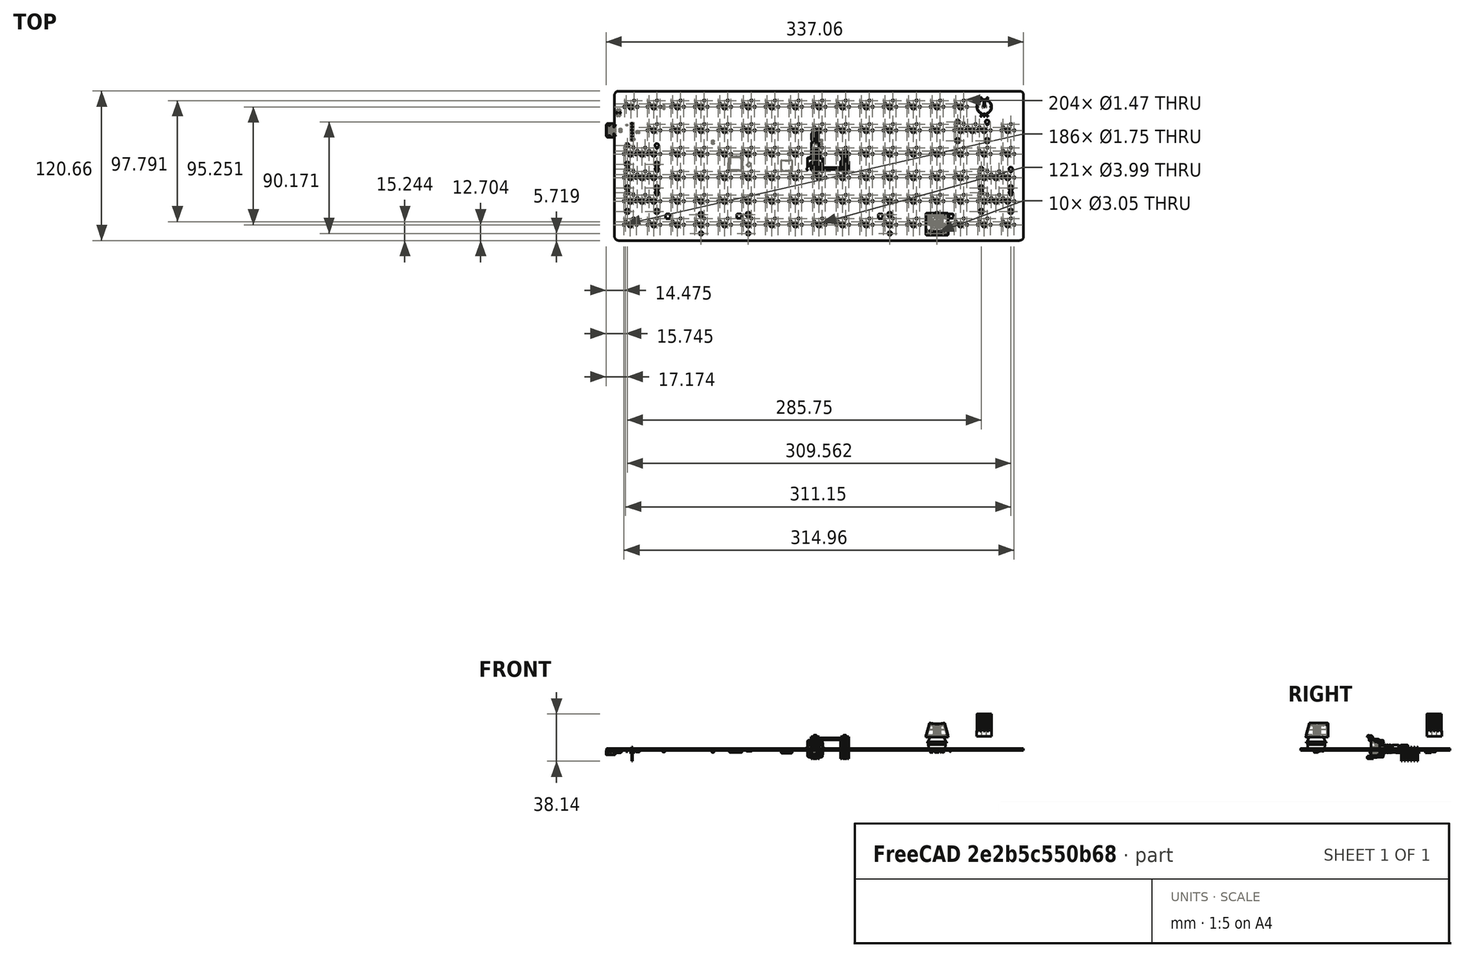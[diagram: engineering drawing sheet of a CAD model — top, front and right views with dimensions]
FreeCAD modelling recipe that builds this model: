
FCSTD DOCUMENT  (FreeCAD 0.19R24291 (Git))
Label: Orthonite87_002
License: All rights reserved
LicenseURL: http://en.wikipedia.org/wiki/All_rights_reserved
objects: App::Link×376, Part::Feature×31, App::Part×8, PartDesign::CoordinateSystem×1, Sketcher::SketchObject×1
note: 33 computed .brp shape members not serialized (recipe doc carries the construction recipe); baked Part::Feature solids carry a one-line shape summary decoded from their .brp

FEATURE [PartDesign::CoordinateSystem] Local_CS_e1db
  AttacherType = Attacher::AttachEngine3D
FEATURE [Part::Feature] Pcb_e1db
  Placement = pos=(-174.625,80.9625,0) rot=(0,0,1;0rad)
  shape: bbox 336.6 x 120.7 x 1.6 mm, 675 faces (baked)
FEATURE [Sketcher::SketchObject] PCB_Sketch_e1db
  FullyConstrained = false
  sketch-geometry (18):
    g0: LineSegment StartX=-168.275 StartY=33.3375 StartZ=0 EndX=-168.275 EndY=23.8125 EndZ=0
    g1: LineSegment StartX=-163.512 StartY=23.0188 StartZ=0 EndX=-162.719 EndY=23.0188 EndZ=0
    g2: LineSegment StartX=-163.512 StartY=34.1313 StartZ=0 EndX=-162.719 EndY=34.1313 EndZ=0
    g3: LineSegment StartX=-167.481 StartY=34.1313 StartZ=0 EndX=-163.512 EndY=34.1313 EndZ=0
    g4: LineSegment StartX=-163.512 StartY=23.0188 StartZ=0 EndX=-167.481 EndY=23.0188 EndZ=0
    g5: LineSegment StartX=-161.925 StartY=22.225 StartZ=0 EndX=-161.925 EndY=-57.15 EndZ=0
    g6: LineSegment StartX=-161.925 StartY=57.15 StartZ=0 EndX=-161.925 EndY=34.925 EndZ=0
    g7: LineSegment StartX=168.275 StartY=-57.15 StartZ=0 EndX=168.275 EndY=57.15 EndZ=0
    g8: LineSegment StartX=-158.75 StartY=-60.325 StartZ=0 EndX=165.1 EndY=-60.325 EndZ=0
    g9: LineSegment StartX=-158.75 StartY=60.325 StartZ=0 EndX=165.1 EndY=60.325 EndZ=0
    g10: ArcOfCircle CenterX=-167.481 CenterY=33.3375 CenterZ=0 NormalX=0 NormalY=0 NormalZ=1 AngleXU=0 Radius=0.79375 StartAngle=1.5708 EndAngle=3.14159
    g11: ArcOfCircle CenterX=-167.481 CenterY=23.8125 CenterZ=0 NormalX=0 NormalY=0 NormalZ=1 AngleXU=0 Radius=0.79375 StartAngle=3.14159 EndAngle=4.71239
    g12: ArcOfCircle CenterX=-162.719 CenterY=22.225 CenterZ=0 NormalX=0 NormalY=0 NormalZ=1 AngleXU=0 Radius=0.79375 StartAngle=0 EndAngle=1.5708
    g13: ArcOfCircle CenterX=-162.719 CenterY=34.925 CenterZ=0 NormalX=0 NormalY=0 NormalZ=1 AngleXU=0 Radius=0.79375 StartAngle=4.71239 EndAngle=6.28319
    g14: ArcOfCircle CenterX=165.1 CenterY=-57.15 CenterZ=0 NormalX=0 NormalY=0 NormalZ=1 AngleXU=0 Radius=3.175 StartAngle=4.71239 EndAngle=6.28319
    g15: ArcOfCircle CenterX=-158.75 CenterY=-57.15 CenterZ=0 NormalX=0 NormalY=0 NormalZ=1 AngleXU=0 Radius=3.175 StartAngle=3.14159 EndAngle=4.71239
    g16: ArcOfCircle CenterX=-158.75 CenterY=57.15 CenterZ=0 NormalX=0 NormalY=0 NormalZ=1 AngleXU=0 Radius=3.175 StartAngle=1.5708 EndAngle=3.14159
    g17: ArcOfCircle CenterX=165.1 CenterY=57.15 CenterZ=0 NormalX=0 NormalY=0 NormalZ=1 AngleXU=0 Radius=3.175 StartAngle=0 EndAngle=1.5708
FEATURE [Part::Feature] Shape  label="K_105_cherry mx_611CBFA4"
  Placement = pos=(98.425,-47.6255,5.5) rot=(0,0.707107,0.707107;3.14159rad)
  shape: bbox 15.64 x 16.33 x 17.85 mm, 92 faces (baked)
FEATURE [Part::Feature] Shape001  label="K_105_MX 轴标准键帽__¨¹_¡À__¡§1__¨¤_611CBFA4[2]"
  Placement = pos=(89.425,-38.1255,9.5) rot=(1,0,0;1.5708rad)
  shape: bbox 18.01 x 18 x 11.38 mm, 348 faces (baked)
FEATURE [App::Link] K_105_cherry_mx_611CBFA4_ln_  label="K_108_105_cherry mx_611DE0BA"
  LinkPlacement = pos=(155.575,-47.6255,5.5) rot=(0,0.707107,0.707107;3.14159rad)
  LinkedObject = -> Shape
  Placement = pos=(155.575,-47.6255,5.5) rot=(0,0.707107,0.707107;3.14159rad)
FEATURE [App::Link] K_105_MX______________________________________1_______611CBFA4_2__ln_  label="K_108_105_MX 轴标准键帽__¨¹_¡À__¡§1__¨¤_611DE0BA[2]"
  LinkPlacement = pos=(146.575,-38.1255,9.5) rot=(1,0,0;1.5708rad)
  LinkedObject = -> Shape001
  Placement = pos=(146.575,-38.1255,9.5) rot=(1,0,0;1.5708rad)
FEATURE [App::Link] K_105_cherry_mx_611CBFA4_ln_001  label="K_107_105_cherry mx_611DE0A5"
  LinkPlacement = pos=(136.525,-47.6255,5.5) rot=(0,0.707107,0.707107;3.14159rad)
  LinkedObject = -> Shape
  Placement = pos=(136.525,-47.6255,5.5) rot=(0,0.707107,0.707107;3.14159rad)
FEATURE [App::Link] K_105_MX______________________________________1_______611CBFA4_2__ln_001  label="K_107_105_MX 轴标准键帽__¨¹_¡À__¡§1__¨¤_611DE0A5[2]"
  LinkPlacement = pos=(127.525,-38.1255,9.5) rot=(1,0,0;1.5708rad)
  LinkedObject = -> Shape001
  Placement = pos=(127.525,-38.1255,9.5) rot=(1,0,0;1.5708rad)
FEATURE [App::Link] K_105_cherry_mx_611CBFA4_ln_002  label="K_106_105_cherry mx_611DE090"
  LinkPlacement = pos=(117.475,-47.6255,5.5) rot=(0,0.707107,0.707107;3.14159rad)
  LinkedObject = -> Shape
  Placement = pos=(117.475,-47.6255,5.5) rot=(0,0.707107,0.707107;3.14159rad)
FEATURE [App::Link] K_105_MX______________________________________1_______611CBFA4_2__ln_002  label="K_106_105_MX 轴标准键帽__¨¹_¡À__¡§1__¨¤_611DE090[2]"
  LinkPlacement = pos=(108.475,-38.1255,9.5) rot=(1,0,0;1.5708rad)
  LinkedObject = -> Shape001
  Placement = pos=(108.475,-38.1255,9.5) rot=(1,0,0;1.5708rad)
FEATURE [App::Link] K_105_cherry_mx_611CBFA4_ln_003  label="K_103_105_cherry mx_611DE023"
  LinkPlacement = pos=(60.325,-47.6255,5.5) rot=(0,0.707107,0.707107;3.14159rad)
  LinkedObject = -> Shape
  Placement = pos=(60.325,-47.6255,5.5) rot=(0,0.707107,0.707107;3.14159rad)
FEATURE [App::Link] K_105_MX______________________________________1_______611CBFA4_2__ln_003  label="K_103_105_MX 轴标准键帽__¨¹_¡À__¡§1__¨¤_611DE023[2]"
  LinkPlacement = pos=(51.325,-38.1255,9.5) rot=(1,0,0;1.5708rad)
  LinkedObject = -> Shape001
  Placement = pos=(51.325,-38.1255,9.5) rot=(1,0,0;1.5708rad)
FEATURE [App::Link] K_105_cherry_mx_611CBFA4_ln_004  label="K_102_105_cherry mx_611DE00E"
  LinkPlacement = pos=(41.275,-47.6255,5.5) rot=(0,0.707107,0.707107;3.14159rad)
  LinkedObject = -> Shape
  Placement = pos=(41.275,-47.6255,5.5) rot=(0,0.707107,0.707107;3.14159rad)
FEATURE [App::Link] K_105_MX______________________________________1_______611CBFA4_2__ln_004  label="K_102_105_MX 轴标准键帽__¨¹_¡À__¡§1__¨¤_611DE00E[2]"
  LinkPlacement = pos=(32.275,-38.1255,9.5) rot=(1,0,0;1.5708rad)
  LinkedObject = -> Shape001
  Placement = pos=(32.275,-38.1255,9.5) rot=(1,0,0;1.5708rad)
FEATURE [App::Link] K_105_cherry_mx_611CBFA4_ln_005  label="K_101_105_cherry mx_611DDFF9"
  LinkPlacement = pos=(22.225,-47.6255,5.5) rot=(0,0.707107,0.707107;3.14159rad)
  LinkedObject = -> Shape
  Placement = pos=(22.225,-47.6255,5.5) rot=(0,0.707107,0.707107;3.14159rad)
FEATURE [App::Link] K_105_MX______________________________________1_______611CBFA4_2__ln_005  label="K_101_105_MX 轴标准键帽__¨¹_¡À__¡§1__¨¤_611DDFF9[2]"
  LinkPlacement = pos=(13.225,-38.1255,9.5) rot=(1,0,0;1.5708rad)
  LinkedObject = -> Shape001
  Placement = pos=(13.225,-38.1255,9.5) rot=(1,0,0;1.5708rad)
FEATURE [App::Link] K_105_cherry_mx_611CBFA4_ln_006  label="K_100_105_cherry mx_611DDFE4"
  LinkPlacement = pos=(3.175,-47.6255,5.5) rot=(0,0.707107,0.707107;3.14159rad)
  LinkedObject = -> Shape
  Placement = pos=(3.175,-47.6255,5.5) rot=(0,0.707107,0.707107;3.14159rad)
FEATURE [App::Link] K_105_MX______________________________________1_______611CBFA4_2__ln_006  label="K_100_105_MX 轴标准键帽__¨¹_¡À__¡§1__¨¤_611DDFE4[2]"
  LinkPlacement = pos=(-5.825,-38.1255,9.5) rot=(1,0,0;1.5708rad)
  LinkedObject = -> Shape001
  Placement = pos=(-5.825,-38.1255,9.5) rot=(1,0,0;1.5708rad)
FEATURE [App::Link] K_105_cherry_mx_611CBFA4_ln_007  label="K_2_105_cherry mx_611DD732"
  LinkPlacement = pos=(-148.717,47.625,5.5) rot=(0,0.707107,0.707107;3.14159rad)
  LinkedObject = -> Shape
  Placement = pos=(-148.717,47.625,5.5) rot=(0,0.707107,0.707107;3.14159rad)
FEATURE [App::Link] K_105_MX______________________________________1_______611CBFA4_2__ln_007  label="K_2_105_MX 轴标准键帽__¨¹_¡À__¡§1__¨¤_611DD732[2]"
  LinkPlacement = pos=(-157.717,57.125,9.5) rot=(1,0,0;1.5708rad)
  LinkedObject = -> Shape001
  Placement = pos=(-157.717,57.125,9.5) rot=(1,0,0;1.5708rad)
FEATURE [App::Link] K_105_cherry_mx_611CBFA4_ln_008  label="K_9_105_cherry mx_611DD7C5"
  LinkPlacement = pos=(-15.875,47.625,5.5) rot=(0,0.707107,0.707107;3.14159rad)
  LinkedObject = -> Shape
  Placement = pos=(-15.875,47.625,5.5) rot=(0,0.707107,0.707107;3.14159rad)
FEATURE [App::Link] K_105_MX______________________________________1_______611CBFA4_2__ln_008  label="K_9_105_MX 轴标准键帽__¨¹_¡À__¡§1__¨¤_611DD7C5[2]"
  LinkPlacement = pos=(-24.875,57.125,9.5) rot=(1,0,0;1.5708rad)
  LinkedObject = -> Shape001
  Placement = pos=(-24.875,57.125,9.5) rot=(1,0,0;1.5708rad)
FEATURE [App::Link] K_105_cherry_mx_611CBFA4_ln_009  label="K_8_105_cherry mx_611DD7B0"
  LinkPlacement = pos=(-34.925,47.625,5.5) rot=(0,0.707107,0.707107;3.14159rad)
  LinkedObject = -> Shape
  Placement = pos=(-34.925,47.625,5.5) rot=(0,0.707107,0.707107;3.14159rad)
FEATURE [App::Link] K_105_MX______________________________________1_______611CBFA4_2__ln_009  label="K_8_105_MX 轴标准键帽__¨¹_¡À__¡§1__¨¤_611DD7B0[2]"
  LinkPlacement = pos=(-43.925,57.125,9.5) rot=(1,0,0;1.5708rad)
  LinkedObject = -> Shape001
  Placement = pos=(-43.925,57.125,9.5) rot=(1,0,0;1.5708rad)
FEATURE [App::Link] K_105_cherry_mx_611CBFA4_ln_010  label="K_7_105_cherry mx_611DD79B"
  LinkPlacement = pos=(-53.975,47.625,5.5) rot=(0,0.707107,0.707107;3.14159rad)
  LinkedObject = -> Shape
  Placement = pos=(-53.975,47.625,5.5) rot=(0,0.707107,0.707107;3.14159rad)
FEATURE [App::Link] K_105_MX______________________________________1_______611CBFA4_2__ln_010  label="K_7_105_MX 轴标准键帽__¨¹_¡À__¡§1__¨¤_611DD79B[2]"
  LinkPlacement = pos=(-62.975,57.125,9.5) rot=(1,0,0;1.5708rad)
  LinkedObject = -> Shape001
  Placement = pos=(-62.975,57.125,9.5) rot=(1,0,0;1.5708rad)
FEATURE [App::Link] K_105_cherry_mx_611CBFA4_ln_011  label="K_6_105_cherry mx_611DD786"
  LinkPlacement = pos=(-73.025,47.625,5.5) rot=(0,0.707107,0.707107;3.14159rad)
  LinkedObject = -> Shape
  Placement = pos=(-73.025,47.625,5.5) rot=(0,0.707107,0.707107;3.14159rad)
FEATURE [App::Link] K_105_MX______________________________________1_______611CBFA4_2__ln_011  label="K_6_105_MX 轴标准键帽__¨¹_¡À__¡§1__¨¤_611DD786[2]"
  LinkPlacement = pos=(-82.025,57.125,9.5) rot=(1,0,0;1.5708rad)
  LinkedObject = -> Shape001
  Placement = pos=(-82.025,57.125,9.5) rot=(1,0,0;1.5708rad)
FEATURE [App::Link] K_105_cherry_mx_611CBFA4_ln_012  label="K_5_105_cherry mx_611DD771"
  LinkPlacement = pos=(-92.075,47.625,5.5) rot=(0,0.707107,0.707107;3.14159rad)
  LinkedObject = -> Shape
  Placement = pos=(-92.075,47.625,5.5) rot=(0,0.707107,0.707107;3.14159rad)
FEATURE [App::Link] K_105_MX______________________________________1_______611CBFA4_2__ln_012  label="K_5_105_MX 轴标准键帽__¨¹_¡À__¡§1__¨¤_611DD771[2]"
  LinkPlacement = pos=(-101.075,57.125,9.5) rot=(1,0,0;1.5708rad)
  LinkedObject = -> Shape001
  Placement = pos=(-101.075,57.125,9.5) rot=(1,0,0;1.5708rad)
FEATURE [App::Link] K_105_cherry_mx_611CBFA4_ln_013  label="K_4_105_cherry mx_611DD75C"
  LinkPlacement = pos=(-111.125,47.625,5.5) rot=(0,0.707107,0.707107;3.14159rad)
  LinkedObject = -> Shape
  Placement = pos=(-111.125,47.625,5.5) rot=(0,0.707107,0.707107;3.14159rad)
FEATURE [App::Link] K_105_MX______________________________________1_______611CBFA4_2__ln_013  label="K_4_105_MX 轴标准键帽__¨¹_¡À__¡§1__¨¤_611DD75C[2]"
  LinkPlacement = pos=(-120.125,57.125,9.5) rot=(1,0,0;1.5708rad)
  LinkedObject = -> Shape001
  Placement = pos=(-120.125,57.125,9.5) rot=(1,0,0;1.5708rad)
FEATURE [App::Link] K_105_cherry_mx_611CBFA4_ln_014  label="K_3_105_cherry mx_611DD747"
  LinkPlacement = pos=(-130.175,47.625,5.5) rot=(0,0.707107,0.707107;3.14159rad)
  LinkedObject = -> Shape
  Placement = pos=(-130.175,47.625,5.5) rot=(0,0.707107,0.707107;3.14159rad)
FEATURE [App::Link] K_105_MX______________________________________1_______611CBFA4_2__ln_014  label="K_3_105_MX 轴标准键帽__¨¹_¡À__¡§1__¨¤_611DD747[2]"
  LinkPlacement = pos=(-139.175,57.125,9.5) rot=(1,0,0;1.5708rad)
  LinkedObject = -> Shape001
  Placement = pos=(-139.175,57.125,9.5) rot=(1,0,0;1.5708rad)
FEATURE [App::Link] K_105_cherry_mx_611CBFA4_ln_015  label="K_33_105_cherry mx_611E8F84"
  LinkPlacement = pos=(155.575,28.575,5.5) rot=(0,0.707107,0.707107;3.14159rad)
  LinkedObject = -> Shape
  Placement = pos=(155.575,28.575,5.5) rot=(0,0.707107,0.707107;3.14159rad)
FEATURE [App::Link] K_105_MX______________________________________1_______611CBFA4_2__ln_015  label="K_33_105_MX 轴标准键帽__¨¹_¡À__¡§1__¨¤_611E8F84[2]"
  LinkPlacement = pos=(146.575,38.075,9.5) rot=(1,0,0;1.5708rad)
  LinkedObject = -> Shape001
  Placement = pos=(146.575,38.075,9.5) rot=(1,0,0;1.5708rad)
FEATURE [App::Link] K_105_cherry_mx_611CBFA4_ln_016  label="K_99_105_cherry mx_611DDFCF"
  LinkPlacement = pos=(-15.875,-47.6255,5.5) rot=(0,0.707107,0.707107;3.14159rad)
  LinkedObject = -> Shape
  Placement = pos=(-15.875,-47.6255,5.5) rot=(0,0.707107,0.707107;3.14159rad)
FEATURE [App::Link] K_105_MX______________________________________1_______611CBFA4_2__ln_016  label="K_99_105_MX 轴标准键帽__¨¹_¡À__¡§1__¨¤_611DDFCF[2]"
  LinkPlacement = pos=(-24.875,-38.1255,9.5) rot=(1,0,0;1.5708rad)
  LinkedObject = -> Shape001
  Placement = pos=(-24.875,-38.1255,9.5) rot=(1,0,0;1.5708rad)
FEATURE [App::Link] K_105_cherry_mx_611CBFA4_ln_017  label="K_98_105_cherry mx_611DDFBA"
  LinkPlacement = pos=(-34.925,-47.6255,5.5) rot=(0,0.707107,0.707107;3.14159rad)
  LinkedObject = -> Shape
  Placement = pos=(-34.925,-47.6255,5.5) rot=(0,0.707107,0.707107;3.14159rad)
FEATURE [App::Link] K_105_MX______________________________________1_______611CBFA4_2__ln_017  label="K_98_105_MX 轴标准键帽__¨¹_¡À__¡§1__¨¤_611DDFBA[2]"
  LinkPlacement = pos=(-43.925,-38.1255,9.5) rot=(1,0,0;1.5708rad)
  LinkedObject = -> Shape001
  Placement = pos=(-43.925,-38.1255,9.5) rot=(1,0,0;1.5708rad)
FEATURE [App::Link] K_105_cherry_mx_611CBFA4_ln_018  label="K_97_105_cherry mx_611DDFA5"
  LinkPlacement = pos=(-53.975,-47.6255,5.5) rot=(0,0.707107,0.707107;3.14159rad)
  LinkedObject = -> Shape
  Placement = pos=(-53.975,-47.6255,5.5) rot=(0,0.707107,0.707107;3.14159rad)
FEATURE [App::Link] K_105_MX______________________________________1_______611CBFA4_2__ln_018  label="K_97_105_MX 轴标准键帽__¨¹_¡À__¡§1__¨¤_611DDFA5[2]"
  LinkPlacement = pos=(-62.975,-38.1255,9.5) rot=(1,0,0;1.5708rad)
  LinkedObject = -> Shape001
  Placement = pos=(-62.975,-38.1255,9.5) rot=(1,0,0;1.5708rad)
FEATURE [App::Link] K_105_cherry_mx_611CBFA4_ln_019  label="K_95_105_cherry mx_611DDF60"
  LinkPlacement = pos=(-92.075,-47.6255,5.5) rot=(0,0.707107,0.707107;3.14159rad)
  LinkedObject = -> Shape
  Placement = pos=(-92.075,-47.6255,5.5) rot=(0,0.707107,0.707107;3.14159rad)
FEATURE [App::Link] K_105_MX______________________________________1_______611CBFA4_2__ln_019  label="K_95_105_MX 轴标准键帽__¨¹_¡À__¡§1__¨¤_611DDF60[2]"
  LinkPlacement = pos=(-101.075,-38.1255,9.5) rot=(1,0,0;1.5708rad)
  LinkedObject = -> Shape001
  Placement = pos=(-101.075,-38.1255,9.5) rot=(1,0,0;1.5708rad)
FEATURE [App::Link] K_105_cherry_mx_611CBFA4_ln_020  label="K_94_105_cherry mx_611DDF4B"
  LinkPlacement = pos=(-111.125,-47.6255,5.5) rot=(0,0.707107,0.707107;3.14159rad)
  LinkedObject = -> Shape
  Placement = pos=(-111.125,-47.6255,5.5) rot=(0,0.707107,0.707107;3.14159rad)
FEATURE [App::Link] K_105_MX______________________________________1_______611CBFA4_2__ln_020  label="K_94_105_MX 轴标准键帽__¨¹_¡À__¡§1__¨¤_611DDF4B[2]"
  LinkPlacement = pos=(-120.125,-38.1255,9.5) rot=(1,0,0;1.5708rad)
  LinkedObject = -> Shape001
  Placement = pos=(-120.125,-38.1255,9.5) rot=(1,0,0;1.5708rad)
FEATURE [App::Link] K_105_cherry_mx_611CBFA4_ln_021  label="K_93_105_cherry mx_611DDF36"
  LinkPlacement = pos=(-130.175,-47.6255,5.5) rot=(0,0.707107,0.707107;3.14159rad)
  LinkedObject = -> Shape
  Placement = pos=(-130.175,-47.6255,5.5) rot=(0,0.707107,0.707107;3.14159rad)
FEATURE [App::Link] K_105_MX______________________________________1_______611CBFA4_2__ln_021  label="K_93_105_MX 轴标准键帽__¨¹_¡À__¡§1__¨¤_611DDF36[2]"
  LinkPlacement = pos=(-139.175,-38.1255,9.5) rot=(1,0,0;1.5708rad)
  LinkedObject = -> Shape001
  Placement = pos=(-139.175,-38.1255,9.5) rot=(1,0,0;1.5708rad)
FEATURE [App::Link] K_105_cherry_mx_611CBFA4_ln_022  label="K_92_105_cherry mx_611DDF21"
  LinkPlacement = pos=(-149.225,-47.6255,5.5) rot=(0,0.707107,0.707107;3.14159rad)
  LinkedObject = -> Shape
  Placement = pos=(-149.225,-47.6255,5.5) rot=(0,0.707107,0.707107;3.14159rad)
FEATURE [App::Link] K_105_MX______________________________________1_______611CBFA4_2__ln_022  label="K_92_105_MX 轴标准键帽__¨¹_¡À__¡§1__¨¤_611DDF21[2]"
  LinkPlacement = pos=(-158.225,-38.1255,9.5) rot=(1,0,0;1.5708rad)
  LinkedObject = -> Shape001
  Placement = pos=(-158.225,-38.1255,9.5) rot=(1,0,0;1.5708rad)
FEATURE [App::Link] K_105_cherry_mx_611CBFA4_ln_023  label="K_88_105_cherry mx_611DDEB2"
  LinkPlacement = pos=(136.525,-28.5755,5.5) rot=(0,0.707107,0.707107;3.14159rad)
  LinkedObject = -> Shape
  Placement = pos=(136.525,-28.5755,5.5) rot=(0,0.707107,0.707107;3.14159rad)
FEATURE [App::Link] K_105_MX______________________________________1_______611CBFA4_2__ln_023  label="K_88_105_MX 轴标准键帽__¨¹_¡À__¡§1__¨¤_611DDEB2[2]"
  LinkPlacement = pos=(127.525,-19.0755,9.5) rot=(1,0,0;1.5708rad)
  LinkedObject = -> Shape001
  Placement = pos=(127.525,-19.0755,9.5) rot=(1,0,0;1.5708rad)
FEATURE [App::Link] K_105_cherry_mx_611CBFA4_ln_024  label="K_87_105_cherry mx_611DDE9D"
  LinkPlacement = pos=(117.475,-28.5755,5.5) rot=(0,0.707107,0.707107;3.14159rad)
  LinkedObject = -> Shape
  Placement = pos=(117.475,-28.5755,5.5) rot=(0,0.707107,0.707107;3.14159rad)
FEATURE [App::Link] K_105_MX______________________________________1_______611CBFA4_2__ln_024  label="K_87_105_MX 轴标准键帽__¨¹_¡À__¡§1__¨¤_611DDE9D[2]"
  LinkPlacement = pos=(108.475,-19.0755,9.5) rot=(1,0,0;1.5708rad)
  LinkedObject = -> Shape001
  Placement = pos=(108.475,-19.0755,9.5) rot=(1,0,0;1.5708rad)
FEATURE [App::Link] K_105_cherry_mx_611CBFA4_ln_025  label="K_86_105_cherry mx_611DDE88"
  LinkPlacement = pos=(98.425,-28.5755,5.5) rot=(0,0.707107,0.707107;3.14159rad)
  LinkedObject = -> Shape
  Placement = pos=(98.425,-28.5755,5.5) rot=(0,0.707107,0.707107;3.14159rad)
FEATURE [App::Link] K_105_MX______________________________________1_______611CBFA4_2__ln_025  label="K_86_105_MX 轴标准键帽__¨¹_¡À__¡§1__¨¤_611DDE88[2]"
  LinkPlacement = pos=(89.425,-19.0755,9.5) rot=(1,0,0;1.5708rad)
  LinkedObject = -> Shape001
  Placement = pos=(89.425,-19.0755,9.5) rot=(1,0,0;1.5708rad)
FEATURE [App::Link] K_105_cherry_mx_611CBFA4_ln_026  label="K_85_105_cherry mx_611DDE73"
  LinkPlacement = pos=(79.375,-28.5755,5.5) rot=(0,0.707107,0.707107;3.14159rad)
  LinkedObject = -> Shape
  Placement = pos=(79.375,-28.5755,5.5) rot=(0,0.707107,0.707107;3.14159rad)
FEATURE [App::Link] K_105_MX______________________________________1_______611CBFA4_2__ln_026  label="K_85_105_MX 轴标准键帽__¨¹_¡À__¡§1__¨¤_611DDE73[2]"
  LinkPlacement = pos=(70.375,-19.0755,9.5) rot=(1,0,0;1.5708rad)
  LinkedObject = -> Shape001
  Placement = pos=(70.375,-19.0755,9.5) rot=(1,0,0;1.5708rad)
FEATURE [App::Link] K_105_cherry_mx_611CBFA4_ln_027  label="K_84_105_cherry mx_611DDE5E"
  LinkPlacement = pos=(60.325,-28.5755,5.5) rot=(0,0.707107,0.707107;3.14159rad)
  LinkedObject = -> Shape
  Placement = pos=(60.325,-28.5755,5.5) rot=(0,0.707107,0.707107;3.14159rad)
FEATURE [App::Link] K_105_MX______________________________________1_______611CBFA4_2__ln_027  label="K_84_105_MX 轴标准键帽__¨¹_¡À__¡§1__¨¤_611DDE5E[2]"
  LinkPlacement = pos=(51.325,-19.0755,9.5) rot=(1,0,0;1.5708rad)
  LinkedObject = -> Shape001
  Placement = pos=(51.325,-19.0755,9.5) rot=(1,0,0;1.5708rad)
FEATURE [App::Link] K_105_cherry_mx_611CBFA4_ln_028  label="K_83_105_cherry mx_611DDE49"
  LinkPlacement = pos=(41.275,-28.5755,5.5) rot=(0,0.707107,0.707107;3.14159rad)
  LinkedObject = -> Shape
  Placement = pos=(41.275,-28.5755,5.5) rot=(0,0.707107,0.707107;3.14159rad)
FEATURE [App::Link] K_105_MX______________________________________1_______611CBFA4_2__ln_028  label="K_83_105_MX 轴标准键帽__¨¹_¡À__¡§1__¨¤_611DDE49[2]"
  LinkPlacement = pos=(32.275,-19.0755,9.5) rot=(1,0,0;1.5708rad)
  LinkedObject = -> Shape001
  Placement = pos=(32.275,-19.0755,9.5) rot=(1,0,0;1.5708rad)
FEATURE [App::Link] K_105_cherry_mx_611CBFA4_ln_029  label="K_82_105_cherry mx_611DDE34"
  LinkPlacement = pos=(22.225,-28.5755,5.5) rot=(0,0.707107,0.707107;3.14159rad)
  LinkedObject = -> Shape
  Placement = pos=(22.225,-28.5755,5.5) rot=(0,0.707107,0.707107;3.14159rad)
FEATURE [App::Link] K_105_MX______________________________________1_______611CBFA4_2__ln_029  label="K_82_105_MX 轴标准键帽__¨¹_¡À__¡§1__¨¤_611DDE34[2]"
  LinkPlacement = pos=(13.225,-19.0755,9.5) rot=(1,0,0;1.5708rad)
  LinkedObject = -> Shape001
  Placement = pos=(13.225,-19.0755,9.5) rot=(1,0,0;1.5708rad)
FEATURE [App::Link] K_105_cherry_mx_611CBFA4_ln_030  label="K_81_105_cherry mx_611DDE1F"
  LinkPlacement = pos=(3.175,-28.5755,5.5) rot=(0,0.707107,0.707107;3.14159rad)
  LinkedObject = -> Shape
  Placement = pos=(3.175,-28.5755,5.5) rot=(0,0.707107,0.707107;3.14159rad)
FEATURE [App::Link] K_105_MX______________________________________1_______611CBFA4_2__ln_030  label="K_81_105_MX 轴标准键帽__¨¹_¡À__¡§1__¨¤_611DDE1F[2]"
  LinkPlacement = pos=(-5.825,-19.0755,9.5) rot=(1,0,0;1.5708rad)
  LinkedObject = -> Shape001
  Placement = pos=(-5.825,-19.0755,9.5) rot=(1,0,0;1.5708rad)
FEATURE [App::Link] K_105_cherry_mx_611CBFA4_ln_031  label="K_80_105_cherry mx_611DDE0A"
  LinkPlacement = pos=(-15.875,-28.5755,5.5) rot=(0,0.707107,0.707107;3.14159rad)
  LinkedObject = -> Shape
  Placement = pos=(-15.875,-28.5755,5.5) rot=(0,0.707107,0.707107;3.14159rad)
FEATURE [App::Link] K_105_MX______________________________________1_______611CBFA4_2__ln_031  label="K_80_105_MX 轴标准键帽__¨¹_¡À__¡§1__¨¤_611DDE0A[2]"
  LinkPlacement = pos=(-24.875,-19.0755,9.5) rot=(1,0,0;1.5708rad)
  LinkedObject = -> Shape001
  Placement = pos=(-24.875,-19.0755,9.5) rot=(1,0,0;1.5708rad)
FEATURE [App::Link] K_105_cherry_mx_611CBFA4_ln_032  label="K_79_105_cherry mx_611DDDF5"
  LinkPlacement = pos=(-34.925,-28.5755,5.5) rot=(0,0.707107,0.707107;3.14159rad)
  LinkedObject = -> Shape
  Placement = pos=(-34.925,-28.5755,5.5) rot=(0,0.707107,0.707107;3.14159rad)
FEATURE [App::Link] K_105_MX______________________________________1_______611CBFA4_2__ln_032  label="K_79_105_MX 轴标准键帽__¨¹_¡À__¡§1__¨¤_611DDDF5[2]"
  LinkPlacement = pos=(-43.925,-19.0755,9.5) rot=(1,0,0;1.5708rad)
  LinkedObject = -> Shape001
  Placement = pos=(-43.925,-19.0755,9.5) rot=(1,0,0;1.5708rad)
FEATURE [App::Link] K_105_cherry_mx_611CBFA4_ln_033  label="K_78_105_cherry mx_611DDDE0"
  LinkPlacement = pos=(-53.975,-28.5755,5.5) rot=(0,0.707107,0.707107;3.14159rad)
  LinkedObject = -> Shape
  Placement = pos=(-53.975,-28.5755,5.5) rot=(0,0.707107,0.707107;3.14159rad)
FEATURE [App::Link] K_105_MX______________________________________1_______611CBFA4_2__ln_033  label="K_78_105_MX 轴标准键帽__¨¹_¡À__¡§1__¨¤_611DDDE0[2]"
  LinkPlacement = pos=(-62.975,-19.0755,9.5) rot=(1,0,0;1.5708rad)
  LinkedObject = -> Shape001
  Placement = pos=(-62.975,-19.0755,9.5) rot=(1,0,0;1.5708rad)
FEATURE [App::Link] K_105_cherry_mx_611CBFA4_ln_034  label="K_77_105_cherry mx_611DDDCB"
  LinkPlacement = pos=(-73.025,-28.5755,5.5) rot=(0,0.707107,0.707107;3.14159rad)
  LinkedObject = -> Shape
  Placement = pos=(-73.025,-28.5755,5.5) rot=(0,0.707107,0.707107;3.14159rad)
FEATURE [App::Link] K_105_MX______________________________________1_______611CBFA4_2__ln_034  label="K_77_105_MX 轴标准键帽__¨¹_¡À__¡§1__¨¤_611DDDCB[2]"
  LinkPlacement = pos=(-82.025,-19.0755,9.5) rot=(1,0,0;1.5708rad)
  LinkedObject = -> Shape001
  Placement = pos=(-82.025,-19.0755,9.5) rot=(1,0,0;1.5708rad)
FEATURE [App::Link] K_105_cherry_mx_611CBFA4_ln_035  label="K_76_105_cherry mx_611DDDB6"
  LinkPlacement = pos=(-92.075,-28.5755,5.5) rot=(0,0.707107,0.707107;3.14159rad)
  LinkedObject = -> Shape
  Placement = pos=(-92.075,-28.5755,5.5) rot=(0,0.707107,0.707107;3.14159rad)
FEATURE [App::Link] K_105_MX______________________________________1_______611CBFA4_2__ln_035  label="K_76_105_MX 轴标准键帽__¨¹_¡À__¡§1__¨¤_611DDDB6[2]"
  LinkPlacement = pos=(-101.075,-19.0755,9.5) rot=(1,0,0;1.5708rad)
  LinkedObject = -> Shape001
  Placement = pos=(-101.075,-19.0755,9.5) rot=(1,0,0;1.5708rad)
FEATURE [App::Link] K_105_cherry_mx_611CBFA4_ln_036  label="K_75_105_cherry mx_611DDDA1"
  LinkPlacement = pos=(-111.125,-28.5755,5.5) rot=(0,0.707107,0.707107;3.14159rad)
  LinkedObject = -> Shape
  Placement = pos=(-111.125,-28.5755,5.5) rot=(0,0.707107,0.707107;3.14159rad)
FEATURE [App::Link] K_105_MX______________________________________1_______611CBFA4_2__ln_036  label="K_75_105_MX 轴标准键帽__¨¹_¡À__¡§1__¨¤_611DDDA1[2]"
  LinkPlacement = pos=(-120.125,-19.0755,9.5) rot=(1,0,0;1.5708rad)
  LinkedObject = -> Shape001
  Placement = pos=(-120.125,-19.0755,9.5) rot=(1,0,0;1.5708rad)
FEATURE [App::Link] K_105_cherry_mx_611CBFA4_ln_037  label="K_73_105_cherry mx_611DDD5C"
  LinkPlacement = pos=(-149.225,-28.5755,5.5) rot=(0,0.707107,0.707107;3.14159rad)
  LinkedObject = -> Shape
  Placement = pos=(-149.225,-28.5755,5.5) rot=(0,0.707107,0.707107;3.14159rad)
FEATURE [App::Link] K_105_MX______________________________________1_______611CBFA4_2__ln_037  label="K_73_105_MX 轴标准键帽__¨¹_¡À__¡§1__¨¤_611DDD5C[2]"
  LinkPlacement = pos=(-158.225,-19.0755,9.5) rot=(1,0,0;1.5708rad)
  LinkedObject = -> Shape001
  Placement = pos=(-158.225,-19.0755,9.5) rot=(1,0,0;1.5708rad)
FEATURE [App::Link] K_105_cherry_mx_611CBFA4_ln_038  label="K_72_105_cherry mx_611DDD47"
  LinkPlacement = pos=(155.575,-28.5755,5.5) rot=(0,0.707107,0.707107;3.14159rad)
  LinkedObject = -> Shape
  Placement = pos=(155.575,-28.5755,5.5) rot=(0,0.707107,0.707107;3.14159rad)
FEATURE [App::Link] K_105_MX______________________________________1_______611CBFA4_2__ln_038  label="K_72_105_MX 轴标准键帽__¨¹_¡À__¡§1__¨¤_611DDD47[2]"
  LinkPlacement = pos=(146.575,-19.0755,9.5) rot=(1,0,0;1.5708rad)
  LinkedObject = -> Shape001
  Placement = pos=(146.575,-19.0755,9.5) rot=(1,0,0;1.5708rad)
FEATURE [App::Link] K_105_cherry_mx_611CBFA4_ln_039  label="K_71_105_cherry mx_611DDD32"
  LinkPlacement = pos=(-130.175,-28.5755,5.5) rot=(0,0.707107,0.707107;3.14159rad)
  LinkedObject = -> Shape
  Placement = pos=(-130.175,-28.5755,5.5) rot=(0,0.707107,0.707107;3.14159rad)
FEATURE [App::Link] K_105_MX______________________________________1_______611CBFA4_2__ln_039  label="K_71_105_MX 轴标准键帽__¨¹_¡À__¡§1__¨¤_611DDD32[2]"
  LinkPlacement = pos=(-139.175,-19.0755,9.5) rot=(1,0,0;1.5708rad)
  LinkedObject = -> Shape001
  Placement = pos=(-139.175,-19.0755,9.5) rot=(1,0,0;1.5708rad)
FEATURE [App::Link] K_105_cherry_mx_611CBFA4_ln_040  label="K_69_105_cherry mx_611DDCED"
  LinkPlacement = pos=(136.525,-9.525,5.5) rot=(0,0.707107,0.707107;3.14159rad)
  LinkedObject = -> Shape
  Placement = pos=(136.525,-9.525,5.5) rot=(0,0.707107,0.707107;3.14159rad)
FEATURE [App::Link] K_105_MX______________________________________1_______611CBFA4_2__ln_040  label="K_69_105_MX 轴标准键帽__¨¹_¡À__¡§1__¨¤_611DDCED[2]"
  LinkPlacement = pos=(127.525,-0.025,9.5) rot=(1,0,0;1.5708rad)
  LinkedObject = -> Shape001
  Placement = pos=(127.525,-0.025,9.5) rot=(1,0,0;1.5708rad)
FEATURE [App::Link] K_105_cherry_mx_611CBFA4_ln_041  label="K_68_105_cherry mx_611DDCD8"
  LinkPlacement = pos=(117.475,-9.525,5.5) rot=(0,0.707107,0.707107;3.14159rad)
  LinkedObject = -> Shape
  Placement = pos=(117.475,-9.525,5.5) rot=(0,0.707107,0.707107;3.14159rad)
FEATURE [App::Link] K_105_MX______________________________________1_______611CBFA4_2__ln_041  label="K_68_105_MX 轴标准键帽__¨¹_¡À__¡§1__¨¤_611DDCD8[2]"
  LinkPlacement = pos=(108.475,-0.025,9.5) rot=(1,0,0;1.5708rad)
  LinkedObject = -> Shape001
  Placement = pos=(108.475,-0.025,9.5) rot=(1,0,0;1.5708rad)
FEATURE [App::Link] K_105_cherry_mx_611CBFA4_ln_042  label="K_67_105_cherry mx_611DDCC3"
  LinkPlacement = pos=(98.425,-9.525,5.5) rot=(0,0.707107,0.707107;3.14159rad)
  LinkedObject = -> Shape
  Placement = pos=(98.425,-9.525,5.5) rot=(0,0.707107,0.707107;3.14159rad)
FEATURE [App::Link] K_105_MX______________________________________1_______611CBFA4_2__ln_042  label="K_67_105_MX 轴标准键帽__¨¹_¡À__¡§1__¨¤_611DDCC3[2]"
  LinkPlacement = pos=(89.425,-0.025,9.5) rot=(1,0,0;1.5708rad)
  LinkedObject = -> Shape001
  Placement = pos=(89.425,-0.025,9.5) rot=(1,0,0;1.5708rad)
FEATURE [App::Link] K_105_cherry_mx_611CBFA4_ln_043  label="K_66_105_cherry mx_611DDCAE"
  LinkPlacement = pos=(79.375,-9.525,5.5) rot=(0,0.707107,0.707107;3.14159rad)
  LinkedObject = -> Shape
  Placement = pos=(79.375,-9.525,5.5) rot=(0,0.707107,0.707107;3.14159rad)
FEATURE [App::Link] K_105_MX______________________________________1_______611CBFA4_2__ln_043  label="K_66_105_MX 轴标准键帽__¨¹_¡À__¡§1__¨¤_611DDCAE[2]"
  LinkPlacement = pos=(70.375,-0.025,9.5) rot=(1,0,0;1.5708rad)
  LinkedObject = -> Shape001
  Placement = pos=(70.375,-0.025,9.5) rot=(1,0,0;1.5708rad)
FEATURE [App::Link] K_105_cherry_mx_611CBFA4_ln_044  label="K_65_105_cherry mx_611DDC99"
  LinkPlacement = pos=(60.325,-9.525,5.5) rot=(0,0.707107,0.707107;3.14159rad)
  LinkedObject = -> Shape
  Placement = pos=(60.325,-9.525,5.5) rot=(0,0.707107,0.707107;3.14159rad)
FEATURE [App::Link] K_105_MX______________________________________1_______611CBFA4_2__ln_044  label="K_65_105_MX 轴标准键帽__¨¹_¡À__¡§1__¨¤_611DDC99[2]"
  LinkPlacement = pos=(51.325,-0.025,9.5) rot=(1,0,0;1.5708rad)
  LinkedObject = -> Shape001
  Placement = pos=(51.325,-0.025,9.5) rot=(1,0,0;1.5708rad)
FEATURE [App::Link] K_105_cherry_mx_611CBFA4_ln_045  label="K_64_105_cherry mx_611DDC84"
  LinkPlacement = pos=(41.275,-9.525,5.5) rot=(0,0.707107,0.707107;3.14159rad)
  LinkedObject = -> Shape
  Placement = pos=(41.275,-9.525,5.5) rot=(0,0.707107,0.707107;3.14159rad)
FEATURE [App::Link] K_105_MX______________________________________1_______611CBFA4_2__ln_045  label="K_64_105_MX 轴标准键帽__¨¹_¡À__¡§1__¨¤_611DDC84[2]"
  LinkPlacement = pos=(32.275,-0.025,9.5) rot=(1,0,0;1.5708rad)
  LinkedObject = -> Shape001
  Placement = pos=(32.275,-0.025,9.5) rot=(1,0,0;1.5708rad)
FEATURE [App::Link] K_105_cherry_mx_611CBFA4_ln_046  label="K_63_105_cherry mx_611DDC6F"
  LinkPlacement = pos=(22.225,-9.525,5.5) rot=(0,0.707107,0.707107;3.14159rad)
  LinkedObject = -> Shape
  Placement = pos=(22.225,-9.525,5.5) rot=(0,0.707107,0.707107;3.14159rad)
FEATURE [App::Link] K_105_MX______________________________________1_______611CBFA4_2__ln_046  label="K_63_105_MX 轴标准键帽__¨¹_¡À__¡§1__¨¤_611DDC6F[2]"
  LinkPlacement = pos=(13.225,-0.025,9.5) rot=(1,0,0;1.5708rad)
  LinkedObject = -> Shape001
  Placement = pos=(13.225,-0.025,9.5) rot=(1,0,0;1.5708rad)
FEATURE [App::Link] K_105_cherry_mx_611CBFA4_ln_047  label="K_62_105_cherry mx_611DDC5A"
  LinkPlacement = pos=(3.175,-9.525,5.5) rot=(0,0.707107,0.707107;3.14159rad)
  LinkedObject = -> Shape
  Placement = pos=(3.175,-9.525,5.5) rot=(0,0.707107,0.707107;3.14159rad)
FEATURE [App::Link] K_105_MX______________________________________1_______611CBFA4_2__ln_047  label="K_62_105_MX 轴标准键帽__¨¹_¡À__¡§1__¨¤_611DDC5A[2]"
  LinkPlacement = pos=(-5.825,-0.025,9.5) rot=(1,0,0;1.5708rad)
  LinkedObject = -> Shape001
  Placement = pos=(-5.825,-0.025,9.5) rot=(1,0,0;1.5708rad)
FEATURE [App::Link] K_105_cherry_mx_611CBFA4_ln_048  label="K_61_105_cherry mx_611DDC45"
  LinkPlacement = pos=(-15.875,-9.525,5.5) rot=(0,0.707107,0.707107;3.14159rad)
  LinkedObject = -> Shape
  Placement = pos=(-15.875,-9.525,5.5) rot=(0,0.707107,0.707107;3.14159rad)
FEATURE [App::Link] K_105_MX______________________________________1_______611CBFA4_2__ln_048  label="K_61_105_MX 轴标准键帽__¨¹_¡À__¡§1__¨¤_611DDC45[2]"
  LinkPlacement = pos=(-24.875,-0.025,9.5) rot=(1,0,0;1.5708rad)
  LinkedObject = -> Shape001
  Placement = pos=(-24.875,-0.025,9.5) rot=(1,0,0;1.5708rad)
FEATURE [App::Link] K_105_cherry_mx_611CBFA4_ln_049  label="K_60_105_cherry mx_611DDC30"
  LinkPlacement = pos=(-34.925,-9.525,5.5) rot=(0,0.707107,0.707107;3.14159rad)
  LinkedObject = -> Shape
  Placement = pos=(-34.925,-9.525,5.5) rot=(0,0.707107,0.707107;3.14159rad)
FEATURE [App::Link] K_105_MX______________________________________1_______611CBFA4_2__ln_049  label="K_60_105_MX 轴标准键帽__¨¹_¡À__¡§1__¨¤_611DDC30[2]"
  LinkPlacement = pos=(-43.925,-0.025,9.5) rot=(1,0,0;1.5708rad)
  LinkedObject = -> Shape001
  Placement = pos=(-43.925,-0.025,9.5) rot=(1,0,0;1.5708rad)
FEATURE [App::Link] K_105_cherry_mx_611CBFA4_ln_050  label="K_59_105_cherry mx_611DDC1B"
  LinkPlacement = pos=(-53.975,-9.525,5.5) rot=(0,0.707107,0.707107;3.14159rad)
  LinkedObject = -> Shape
  Placement = pos=(-53.975,-9.525,5.5) rot=(0,0.707107,0.707107;3.14159rad)
FEATURE [App::Link] K_105_MX______________________________________1_______611CBFA4_2__ln_050  label="K_59_105_MX 轴标准键帽__¨¹_¡À__¡§1__¨¤_611DDC1B[2]"
  LinkPlacement = pos=(-62.975,-0.025,9.5) rot=(1,0,0;1.5708rad)
  LinkedObject = -> Shape001
  Placement = pos=(-62.975,-0.025,9.5) rot=(1,0,0;1.5708rad)
FEATURE [App::Link] K_105_cherry_mx_611CBFA4_ln_051  label="K_58_105_cherry mx_611DDC06"
  LinkPlacement = pos=(-73.025,-9.525,5.5) rot=(0,0.707107,0.707107;3.14159rad)
  LinkedObject = -> Shape
  Placement = pos=(-73.025,-9.525,5.5) rot=(0,0.707107,0.707107;3.14159rad)
FEATURE [App::Link] K_105_MX______________________________________1_______611CBFA4_2__ln_051  label="K_58_105_MX 轴标准键帽__¨¹_¡À__¡§1__¨¤_611DDC06[2]"
  LinkPlacement = pos=(-82.025,-0.025,9.5) rot=(1,0,0;1.5708rad)
  LinkedObject = -> Shape001
  Placement = pos=(-82.025,-0.025,9.5) rot=(1,0,0;1.5708rad)
FEATURE [App::Link] K_105_cherry_mx_611CBFA4_ln_052  label="K_57_105_cherry mx_611DDBF1"
  LinkPlacement = pos=(-92.075,-9.525,5.5) rot=(0,0.707107,0.707107;3.14159rad)
  LinkedObject = -> Shape
  Placement = pos=(-92.075,-9.525,5.5) rot=(0,0.707107,0.707107;3.14159rad)
FEATURE [App::Link] K_105_MX______________________________________1_______611CBFA4_2__ln_052  label="K_57_105_MX 轴标准键帽__¨¹_¡À__¡§1__¨¤_611DDBF1[2]"
  LinkPlacement = pos=(-101.075,-0.025,9.5) rot=(1,0,0;1.5708rad)
  LinkedObject = -> Shape001
  Placement = pos=(-101.075,-0.025,9.5) rot=(1,0,0;1.5708rad)
FEATURE [App::Link] K_105_cherry_mx_611CBFA4_ln_053  label="K_56_105_cherry mx_611DDBDC"
  LinkPlacement = pos=(-111.125,-9.525,5.5) rot=(0,0.707107,0.707107;3.14159rad)
  LinkedObject = -> Shape
  Placement = pos=(-111.125,-9.525,5.5) rot=(0,0.707107,0.707107;3.14159rad)
FEATURE [App::Link] K_105_MX______________________________________1_______611CBFA4_2__ln_053  label="K_56_105_MX 轴标准键帽__¨¹_¡À__¡§1__¨¤_611DDBDC[2]"
  LinkPlacement = pos=(-120.125,-0.025,9.5) rot=(1,0,0;1.5708rad)
  LinkedObject = -> Shape001
  Placement = pos=(-120.125,-0.025,9.5) rot=(1,0,0;1.5708rad)
FEATURE [App::Link] K_105_cherry_mx_611CBFA4_ln_054  label="K_54_105_cherry mx_611DDB97"
  LinkPlacement = pos=(-149.225,-9.525,5.5) rot=(0,0.707107,0.707107;3.14159rad)
  LinkedObject = -> Shape
  Placement = pos=(-149.225,-9.525,5.5) rot=(0,0.707107,0.707107;3.14159rad)
FEATURE [App::Link] K_105_MX______________________________________1_______611CBFA4_2__ln_054  label="K_54_105_MX 轴标准键帽__¨¹_¡À__¡§1__¨¤_611DDB97[2]"
  LinkPlacement = pos=(-158.225,-0.025,9.5) rot=(1,0,0;1.5708rad)
  LinkedObject = -> Shape001
  Placement = pos=(-158.225,-0.025,9.5) rot=(1,0,0;1.5708rad)
FEATURE [App::Link] K_105_cherry_mx_611CBFA4_ln_055  label="K_53_105_cherry mx_611DDB82"
  LinkPlacement = pos=(155.575,-9.525,5.5) rot=(0,0.707107,0.707107;3.14159rad)
  LinkedObject = -> Shape
  Placement = pos=(155.575,-9.525,5.5) rot=(0,0.707107,0.707107;3.14159rad)
FEATURE [App::Link] K_105_MX______________________________________1_______611CBFA4_2__ln_055  label="K_53_105_MX 轴标准键帽__¨¹_¡À__¡§1__¨¤_611DDB82[2]"
  LinkPlacement = pos=(146.575,-0.025,9.5) rot=(1,0,0;1.5708rad)
  LinkedObject = -> Shape001
  Placement = pos=(146.575,-0.025,9.5) rot=(1,0,0;1.5708rad)
FEATURE [App::Link] K_105_cherry_mx_611CBFA4_ln_056  label="K_52_105_cherry mx_611DDB6D"
  LinkPlacement = pos=(-130.175,-9.525,5.5) rot=(0,0.707107,0.707107;3.14159rad)
  LinkedObject = -> Shape
  Placement = pos=(-130.175,-9.525,5.5) rot=(0,0.707107,0.707107;3.14159rad)
FEATURE [App::Link] K_105_MX______________________________________1_______611CBFA4_2__ln_056  label="K_52_105_MX 轴标准键帽__¨¹_¡À__¡§1__¨¤_611DDB6D[2]"
  LinkPlacement = pos=(-139.175,-0.025,9.5) rot=(1,0,0;1.5708rad)
  LinkedObject = -> Shape001
  Placement = pos=(-139.175,-0.025,9.5) rot=(1,0,0;1.5708rad)
FEATURE [App::Link] K_105_cherry_mx_611CBFA4_ln_057  label="K_51_105_cherry mx_611DDB58"
  LinkPlacement = pos=(155.575,9.525,5.5) rot=(0,0.707107,0.707107;3.14159rad)
  LinkedObject = -> Shape
  Placement = pos=(155.575,9.525,5.5) rot=(0,0.707107,0.707107;3.14159rad)
FEATURE [App::Link] K_105_MX______________________________________1_______611CBFA4_2__ln_057  label="K_51_105_MX 轴标准键帽__¨¹_¡À__¡§1__¨¤_611DDB58[2]"
  LinkPlacement = pos=(146.575,19.025,9.5) rot=(1,0,0;1.5708rad)
  LinkedObject = -> Shape001
  Placement = pos=(146.575,19.025,9.5) rot=(1,0,0;1.5708rad)
FEATURE [App::Link] K_105_cherry_mx_611CBFA4_ln_058  label="K_50_105_cherry mx_611DDB43"
  LinkPlacement = pos=(136.525,9.525,5.5) rot=(0,0.707107,0.707107;3.14159rad)
  LinkedObject = -> Shape
  Placement = pos=(136.525,9.525,5.5) rot=(0,0.707107,0.707107;3.14159rad)
FEATURE [App::Link] K_105_MX______________________________________1_______611CBFA4_2__ln_058  label="K_50_105_MX 轴标准键帽__¨¹_¡À__¡§1__¨¤_611DDB43[2]"
  LinkPlacement = pos=(127.525,19.025,9.5) rot=(1,0,0;1.5708rad)
  LinkedObject = -> Shape001
  Placement = pos=(127.525,19.025,9.5) rot=(1,0,0;1.5708rad)
FEATURE [App::Link] K_105_cherry_mx_611CBFA4_ln_059  label="K_49_105_cherry mx_611DDB2E"
  LinkPlacement = pos=(117.475,9.525,5.5) rot=(0,0.707107,0.707107;3.14159rad)
  LinkedObject = -> Shape
  Placement = pos=(117.475,9.525,5.5) rot=(0,0.707107,0.707107;3.14159rad)
FEATURE [App::Link] K_105_MX______________________________________1_______611CBFA4_2__ln_059  label="K_49_105_MX 轴标准键帽__¨¹_¡À__¡§1__¨¤_611DDB2E[2]"
  LinkPlacement = pos=(108.475,19.025,9.5) rot=(1,0,0;1.5708rad)
  LinkedObject = -> Shape001
  Placement = pos=(108.475,19.025,9.5) rot=(1,0,0;1.5708rad)
FEATURE [App::Link] K_105_cherry_mx_611CBFA4_ln_060  label="K_48_105_cherry mx_611DDB19"
  LinkPlacement = pos=(98.425,9.525,5.5) rot=(0,0.707107,0.707107;3.14159rad)
  LinkedObject = -> Shape
  Placement = pos=(98.425,9.525,5.5) rot=(0,0.707107,0.707107;3.14159rad)
FEATURE [App::Link] K_105_MX______________________________________1_______611CBFA4_2__ln_060  label="K_48_105_MX 轴标准键帽__¨¹_¡À__¡§1__¨¤_611DDB19[2]"
  LinkPlacement = pos=(89.425,19.025,9.5) rot=(1,0,0;1.5708rad)
  LinkedObject = -> Shape001
  Placement = pos=(89.425,19.025,9.5) rot=(1,0,0;1.5708rad)
FEATURE [App::Link] K_105_cherry_mx_611CBFA4_ln_061  label="K_47_105_cherry mx_611DDB04"
  LinkPlacement = pos=(79.375,9.525,5.5) rot=(0,0.707107,0.707107;3.14159rad)
  LinkedObject = -> Shape
  Placement = pos=(79.375,9.525,5.5) rot=(0,0.707107,0.707107;3.14159rad)
FEATURE [App::Link] K_105_MX______________________________________1_______611CBFA4_2__ln_061  label="K_47_105_MX 轴标准键帽__¨¹_¡À__¡§1__¨¤_611DDB04[2]"
  LinkPlacement = pos=(70.375,19.025,9.5) rot=(1,0,0;1.5708rad)
  LinkedObject = -> Shape001
  Placement = pos=(70.375,19.025,9.5) rot=(1,0,0;1.5708rad)
FEATURE [App::Link] K_105_cherry_mx_611CBFA4_ln_062  label="K_46_105_cherry mx_611DDAEF"
  LinkPlacement = pos=(60.325,9.525,5.5) rot=(0,0.707107,0.707107;3.14159rad)
  LinkedObject = -> Shape
  Placement = pos=(60.325,9.525,5.5) rot=(0,0.707107,0.707107;3.14159rad)
FEATURE [App::Link] K_105_MX______________________________________1_______611CBFA4_2__ln_062  label="K_46_105_MX 轴标准键帽__¨¹_¡À__¡§1__¨¤_611DDAEF[2]"
  LinkPlacement = pos=(51.325,19.025,9.5) rot=(1,0,0;1.5708rad)
  LinkedObject = -> Shape001
  Placement = pos=(51.325,19.025,9.5) rot=(1,0,0;1.5708rad)
FEATURE [App::Link] K_105_cherry_mx_611CBFA4_ln_063  label="K_45_105_cherry mx_611DDADA"
  LinkPlacement = pos=(41.275,9.525,5.5) rot=(0,0.707107,0.707107;3.14159rad)
  LinkedObject = -> Shape
  Placement = pos=(41.275,9.525,5.5) rot=(0,0.707107,0.707107;3.14159rad)
FEATURE [App::Link] K_105_MX______________________________________1_______611CBFA4_2__ln_063  label="K_45_105_MX 轴标准键帽__¨¹_¡À__¡§1__¨¤_611DDADA[2]"
  LinkPlacement = pos=(32.275,19.025,9.5) rot=(1,0,0;1.5708rad)
  LinkedObject = -> Shape001
  Placement = pos=(32.275,19.025,9.5) rot=(1,0,0;1.5708rad)
FEATURE [App::Link] K_105_cherry_mx_611CBFA4_ln_064  label="K_44_105_cherry mx_611DDAC5"
  LinkPlacement = pos=(22.225,9.525,5.5) rot=(0,0.707107,0.707107;3.14159rad)
  LinkedObject = -> Shape
  Placement = pos=(22.225,9.525,5.5) rot=(0,0.707107,0.707107;3.14159rad)
FEATURE [App::Link] K_105_MX______________________________________1_______611CBFA4_2__ln_064  label="K_44_105_MX 轴标准键帽__¨¹_¡À__¡§1__¨¤_611DDAC5[2]"
  LinkPlacement = pos=(13.225,19.025,9.5) rot=(1,0,0;1.5708rad)
  LinkedObject = -> Shape001
  Placement = pos=(13.225,19.025,9.5) rot=(1,0,0;1.5708rad)
FEATURE [App::Link] K_105_cherry_mx_611CBFA4_ln_065  label="K_43_105_cherry mx_611DDAB0"
  LinkPlacement = pos=(3.175,9.525,5.5) rot=(0,0.707107,0.707107;3.14159rad)
  LinkedObject = -> Shape
  Placement = pos=(3.175,9.525,5.5) rot=(0,0.707107,0.707107;3.14159rad)
FEATURE [App::Link] K_105_MX______________________________________1_______611CBFA4_2__ln_065  label="K_43_105_MX 轴标准键帽__¨¹_¡À__¡§1__¨¤_611DDAB0[2]"
  LinkPlacement = pos=(-5.825,19.025,9.5) rot=(1,0,0;1.5708rad)
  LinkedObject = -> Shape001
  Placement = pos=(-5.825,19.025,9.5) rot=(1,0,0;1.5708rad)
FEATURE [App::Link] K_105_cherry_mx_611CBFA4_ln_066  label="K_42_105_cherry mx_611DDA9B"
  LinkPlacement = pos=(-15.875,9.525,5.5) rot=(0,0.707107,0.707107;3.14159rad)
  LinkedObject = -> Shape
  Placement = pos=(-15.875,9.525,5.5) rot=(0,0.707107,0.707107;3.14159rad)
FEATURE [App::Link] K_105_MX______________________________________1_______611CBFA4_2__ln_066  label="K_42_105_MX 轴标准键帽__¨¹_¡À__¡§1__¨¤_611DDA9B[2]"
  LinkPlacement = pos=(-24.875,19.025,9.5) rot=(1,0,0;1.5708rad)
  LinkedObject = -> Shape001
  Placement = pos=(-24.875,19.025,9.5) rot=(1,0,0;1.5708rad)
FEATURE [App::Link] K_105_cherry_mx_611CBFA4_ln_067  label="K_41_105_cherry mx_611DDA86"
  LinkPlacement = pos=(-34.925,9.525,5.5) rot=(0,0.707107,0.707107;3.14159rad)
  LinkedObject = -> Shape
  Placement = pos=(-34.925,9.525,5.5) rot=(0,0.707107,0.707107;3.14159rad)
FEATURE [App::Link] K_105_MX______________________________________1_______611CBFA4_2__ln_067  label="K_41_105_MX 轴标准键帽__¨¹_¡À__¡§1__¨¤_611DDA86[2]"
  LinkPlacement = pos=(-43.925,19.025,9.5) rot=(1,0,0;1.5708rad)
  LinkedObject = -> Shape001
  Placement = pos=(-43.925,19.025,9.5) rot=(1,0,0;1.5708rad)
FEATURE [App::Link] K_105_cherry_mx_611CBFA4_ln_068  label="K_40_105_cherry mx_611DDA71"
  LinkPlacement = pos=(-53.975,9.525,5.5) rot=(0,0.707107,0.707107;3.14159rad)
  LinkedObject = -> Shape
  Placement = pos=(-53.975,9.525,5.5) rot=(0,0.707107,0.707107;3.14159rad)
FEATURE [App::Link] K_105_MX______________________________________1_______611CBFA4_2__ln_068  label="K_40_105_MX 轴标准键帽__¨¹_¡À__¡§1__¨¤_611DDA71[2]"
  LinkPlacement = pos=(-62.975,19.025,9.5) rot=(1,0,0;1.5708rad)
  LinkedObject = -> Shape001
  Placement = pos=(-62.975,19.025,9.5) rot=(1,0,0;1.5708rad)
FEATURE [App::Link] K_105_cherry_mx_611CBFA4_ln_069  label="K_39_105_cherry mx_611DDA5C"
  LinkPlacement = pos=(-73.025,9.525,5.5) rot=(0,0.707107,0.707107;3.14159rad)
  LinkedObject = -> Shape
  Placement = pos=(-73.025,9.525,5.5) rot=(0,0.707107,0.707107;3.14159rad)
FEATURE [App::Link] K_105_MX______________________________________1_______611CBFA4_2__ln_069  label="K_39_105_MX 轴标准键帽__¨¹_¡À__¡§1__¨¤_611DDA5C[2]"
  LinkPlacement = pos=(-82.025,19.025,9.5) rot=(1,0,0;1.5708rad)
  LinkedObject = -> Shape001
  Placement = pos=(-82.025,19.025,9.5) rot=(1,0,0;1.5708rad)
FEATURE [App::Link] K_105_cherry_mx_611CBFA4_ln_070  label="K_38_105_cherry mx_611DDA47"
  LinkPlacement = pos=(-92.075,9.525,5.5) rot=(0,0.707107,0.707107;3.14159rad)
  LinkedObject = -> Shape
  Placement = pos=(-92.075,9.525,5.5) rot=(0,0.707107,0.707107;3.14159rad)
FEATURE [App::Link] K_105_MX______________________________________1_______611CBFA4_2__ln_070  label="K_38_105_MX 轴标准键帽__¨¹_¡À__¡§1__¨¤_611DDA47[2]"
  LinkPlacement = pos=(-101.075,19.025,9.5) rot=(1,0,0;1.5708rad)
  LinkedObject = -> Shape001
  Placement = pos=(-101.075,19.025,9.5) rot=(1,0,0;1.5708rad)
FEATURE [App::Link] K_105_cherry_mx_611CBFA4_ln_071  label="K_37_105_cherry mx_611DDA32"
  LinkPlacement = pos=(-111.125,9.525,5.5) rot=(0,0.707107,0.707107;3.14159rad)
  LinkedObject = -> Shape
  Placement = pos=(-111.125,9.525,5.5) rot=(0,0.707107,0.707107;3.14159rad)
FEATURE [App::Link] K_105_MX______________________________________1_______611CBFA4_2__ln_071  label="K_37_105_MX 轴标准键帽__¨¹_¡À__¡§1__¨¤_611DDA32[2]"
  LinkPlacement = pos=(-120.125,19.025,9.5) rot=(1,0,0;1.5708rad)
  LinkedObject = -> Shape001
  Placement = pos=(-120.125,19.025,9.5) rot=(1,0,0;1.5708rad)
FEATURE [App::Link] K_105_cherry_mx_611CBFA4_ln_072  label="K_35_105_cherry mx_611DD9ED"
  LinkPlacement = pos=(-149.225,9.525,5.5) rot=(0,0.707107,0.707107;3.14159rad)
  LinkedObject = -> Shape
  Placement = pos=(-149.225,9.525,5.5) rot=(0,0.707107,0.707107;3.14159rad)
FEATURE [App::Link] K_105_MX______________________________________1_______611CBFA4_2__ln_072  label="K_35_105_MX 轴标准键帽__¨¹_¡À__¡§1__¨¤_611DD9ED[2]"
  LinkPlacement = pos=(-158.225,19.025,9.5) rot=(1,0,0;1.5708rad)
  LinkedObject = -> Shape001
  Placement = pos=(-158.225,19.025,9.5) rot=(1,0,0;1.5708rad)
FEATURE [App::Link] K_105_cherry_mx_611CBFA4_ln_073  label="K_34_105_cherry mx_611DD9D8"
  LinkPlacement = pos=(-130.175,9.525,5.5) rot=(0,0.707107,0.707107;3.14159rad)
  LinkedObject = -> Shape
  Placement = pos=(-130.175,9.525,5.5) rot=(0,0.707107,0.707107;3.14159rad)
FEATURE [App::Link] K_105_MX______________________________________1_______611CBFA4_2__ln_073  label="K_34_105_MX 轴标准键帽__¨¹_¡À__¡§1__¨¤_611DD9D8[2]"
  LinkPlacement = pos=(-139.175,19.025,9.5) rot=(1,0,0;1.5708rad)
  LinkedObject = -> Shape001
  Placement = pos=(-139.175,19.025,9.5) rot=(1,0,0;1.5708rad)
FEATURE [App::Link] K_105_cherry_mx_611CBFA4_ln_074  label="K_31_105_cherry mx_611DD993"
  LinkPlacement = pos=(117.475,28.575,5.5) rot=(0,0.707107,0.707107;3.14159rad)
  LinkedObject = -> Shape
  Placement = pos=(117.475,28.575,5.5) rot=(0,0.707107,0.707107;3.14159rad)
FEATURE [App::Link] K_105_MX______________________________________1_______611CBFA4_2__ln_074  label="K_31_105_MX 轴标准键帽__¨¹_¡À__¡§1__¨¤_611DD993[2]"
  LinkPlacement = pos=(108.475,38.075,9.5) rot=(1,0,0;1.5708rad)
  LinkedObject = -> Shape001
  Placement = pos=(108.475,38.075,9.5) rot=(1,0,0;1.5708rad)
FEATURE [App::Link] K_105_cherry_mx_611CBFA4_ln_075  label="K_30_105_cherry mx_611DD97E"
  LinkPlacement = pos=(98.425,28.575,5.5) rot=(0,0.707107,0.707107;3.14159rad)
  LinkedObject = -> Shape
  Placement = pos=(98.425,28.575,5.5) rot=(0,0.707107,0.707107;3.14159rad)
FEATURE [App::Link] K_105_MX______________________________________1_______611CBFA4_2__ln_075  label="K_30_105_MX 轴标准键帽__¨¹_¡À__¡§1__¨¤_611DD97E[2]"
  LinkPlacement = pos=(89.425,38.075,9.5) rot=(1,0,0;1.5708rad)
  LinkedObject = -> Shape001
  Placement = pos=(89.425,38.075,9.5) rot=(1,0,0;1.5708rad)
FEATURE [App::Link] K_105_cherry_mx_611CBFA4_ln_076  label="K_29_105_cherry mx_611DD969"
  LinkPlacement = pos=(79.375,28.575,5.5) rot=(0,0.707107,0.707107;3.14159rad)
  LinkedObject = -> Shape
  Placement = pos=(79.375,28.575,5.5) rot=(0,0.707107,0.707107;3.14159rad)
FEATURE [App::Link] K_105_MX______________________________________1_______611CBFA4_2__ln_076  label="K_29_105_MX 轴标准键帽__¨¹_¡À__¡§1__¨¤_611DD969[2]"
  LinkPlacement = pos=(70.375,38.075,9.5) rot=(1,0,0;1.5708rad)
  LinkedObject = -> Shape001
  Placement = pos=(70.375,38.075,9.5) rot=(1,0,0;1.5708rad)
FEATURE [App::Link] K_105_cherry_mx_611CBFA4_ln_077  label="K_28_105_cherry mx_611DD954"
  LinkPlacement = pos=(60.325,28.575,5.5) rot=(0,0.707107,0.707107;3.14159rad)
  LinkedObject = -> Shape
  Placement = pos=(60.325,28.575,5.5) rot=(0,0.707107,0.707107;3.14159rad)
FEATURE [App::Link] K_105_MX______________________________________1_______611CBFA4_2__ln_077  label="K_28_105_MX 轴标准键帽__¨¹_¡À__¡§1__¨¤_611DD954[2]"
  LinkPlacement = pos=(51.325,38.075,9.5) rot=(1,0,0;1.5708rad)
  LinkedObject = -> Shape001
  Placement = pos=(51.325,38.075,9.5) rot=(1,0,0;1.5708rad)
FEATURE [App::Link] K_105_cherry_mx_611CBFA4_ln_078  label="K_27_105_cherry mx_611DD93F"
  LinkPlacement = pos=(41.275,28.575,5.5) rot=(0,0.707107,0.707107;3.14159rad)
  LinkedObject = -> Shape
  Placement = pos=(41.275,28.575,5.5) rot=(0,0.707107,0.707107;3.14159rad)
FEATURE [App::Link] K_105_MX______________________________________1_______611CBFA4_2__ln_078  label="K_27_105_MX 轴标准键帽__¨¹_¡À__¡§1__¨¤_611DD93F[2]"
  LinkPlacement = pos=(32.275,38.075,9.5) rot=(1,0,0;1.5708rad)
  LinkedObject = -> Shape001
  Placement = pos=(32.275,38.075,9.5) rot=(1,0,0;1.5708rad)
FEATURE [App::Link] K_105_cherry_mx_611CBFA4_ln_079  label="K_26_105_cherry mx_611DD92A"
  LinkPlacement = pos=(22.225,28.575,5.5) rot=(0,0.707107,0.707107;3.14159rad)
  LinkedObject = -> Shape
  Placement = pos=(22.225,28.575,5.5) rot=(0,0.707107,0.707107;3.14159rad)
FEATURE [App::Link] K_105_MX______________________________________1_______611CBFA4_2__ln_079  label="K_26_105_MX 轴标准键帽__¨¹_¡À__¡§1__¨¤_611DD92A[2]"
  LinkPlacement = pos=(13.225,38.075,9.5) rot=(1,0,0;1.5708rad)
  LinkedObject = -> Shape001
  Placement = pos=(13.225,38.075,9.5) rot=(1,0,0;1.5708rad)
FEATURE [App::Link] K_105_cherry_mx_611CBFA4_ln_080  label="K_25_105_cherry mx_611DD915"
  LinkPlacement = pos=(3.175,28.575,5.5) rot=(0,0.707107,0.707107;3.14159rad)
  LinkedObject = -> Shape
  Placement = pos=(3.175,28.575,5.5) rot=(0,0.707107,0.707107;3.14159rad)
FEATURE [App::Link] K_105_MX______________________________________1_______611CBFA4_2__ln_080  label="K_25_105_MX 轴标准键帽__¨¹_¡À__¡§1__¨¤_611DD915[2]"
  LinkPlacement = pos=(-5.825,38.075,9.5) rot=(1,0,0;1.5708rad)
  LinkedObject = -> Shape001
  Placement = pos=(-5.825,38.075,9.5) rot=(1,0,0;1.5708rad)
FEATURE [App::Link] K_105_cherry_mx_611CBFA4_ln_081  label="K_24_105_cherry mx_611DD900"
  LinkPlacement = pos=(-15.875,28.575,5.5) rot=(0,0.707107,0.707107;3.14159rad)
  LinkedObject = -> Shape
  Placement = pos=(-15.875,28.575,5.5) rot=(0,0.707107,0.707107;3.14159rad)
FEATURE [App::Link] K_105_MX______________________________________1_______611CBFA4_2__ln_081  label="K_24_105_MX 轴标准键帽__¨¹_¡À__¡§1__¨¤_611DD900[2]"
  LinkPlacement = pos=(-24.875,38.075,9.5) rot=(1,0,0;1.5708rad)
  LinkedObject = -> Shape001
  Placement = pos=(-24.875,38.075,9.5) rot=(1,0,0;1.5708rad)
FEATURE [App::Link] K_105_cherry_mx_611CBFA4_ln_082  label="K_23_105_cherry mx_611DD8EB"
  LinkPlacement = pos=(-34.925,28.575,5.5) rot=(0,0.707107,0.707107;3.14159rad)
  LinkedObject = -> Shape
  Placement = pos=(-34.925,28.575,5.5) rot=(0,0.707107,0.707107;3.14159rad)
FEATURE [App::Link] K_105_MX______________________________________1_______611CBFA4_2__ln_082  label="K_23_105_MX 轴标准键帽__¨¹_¡À__¡§1__¨¤_611DD8EB[2]"
  LinkPlacement = pos=(-43.925,38.075,9.5) rot=(1,0,0;1.5708rad)
  LinkedObject = -> Shape001
  Placement = pos=(-43.925,38.075,9.5) rot=(1,0,0;1.5708rad)
FEATURE [App::Link] K_105_cherry_mx_611CBFA4_ln_083  label="K_22_105_cherry mx_611DD8D6"
  LinkPlacement = pos=(-53.975,28.575,5.5) rot=(0,0.707107,0.707107;3.14159rad)
  LinkedObject = -> Shape
  Placement = pos=(-53.975,28.575,5.5) rot=(0,0.707107,0.707107;3.14159rad)
FEATURE [App::Link] K_105_MX______________________________________1_______611CBFA4_2__ln_083  label="K_22_105_MX 轴标准键帽__¨¹_¡À__¡§1__¨¤_611DD8D6[2]"
  LinkPlacement = pos=(-62.975,38.075,9.5) rot=(1,0,0;1.5708rad)
  LinkedObject = -> Shape001
  Placement = pos=(-62.975,38.075,9.5) rot=(1,0,0;1.5708rad)
FEATURE [App::Link] K_105_cherry_mx_611CBFA4_ln_084  label="K_21_105_cherry mx_611DD8C1"
  LinkPlacement = pos=(-73.025,28.575,5.5) rot=(0,0.707107,0.707107;3.14159rad)
  LinkedObject = -> Shape
  Placement = pos=(-73.025,28.575,5.5) rot=(0,0.707107,0.707107;3.14159rad)
FEATURE [App::Link] K_105_MX______________________________________1_______611CBFA4_2__ln_084  label="K_21_105_MX 轴标准键帽__¨¹_¡À__¡§1__¨¤_611DD8C1[2]"
  LinkPlacement = pos=(-82.025,38.075,9.5) rot=(1,0,0;1.5708rad)
  LinkedObject = -> Shape001
  Placement = pos=(-82.025,38.075,9.5) rot=(1,0,0;1.5708rad)
FEATURE [App::Link] K_105_cherry_mx_611CBFA4_ln_085  label="K_20_105_cherry mx_611DD8AC"
  LinkPlacement = pos=(-92.075,28.575,5.5) rot=(0,0.707107,0.707107;3.14159rad)
  LinkedObject = -> Shape
  Placement = pos=(-92.075,28.575,5.5) rot=(0,0.707107,0.707107;3.14159rad)
FEATURE [App::Link] K_105_MX______________________________________1_______611CBFA4_2__ln_085  label="K_20_105_MX 轴标准键帽__¨¹_¡À__¡§1__¨¤_611DD8AC[2]"
  LinkPlacement = pos=(-101.075,38.075,9.5) rot=(1,0,0;1.5708rad)
  LinkedObject = -> Shape001
  Placement = pos=(-101.075,38.075,9.5) rot=(1,0,0;1.5708rad)
FEATURE [App::Link] K_105_cherry_mx_611CBFA4_ln_086  label="K_19_105_cherry mx_611DD897"
  LinkPlacement = pos=(-111.125,28.575,5.5) rot=(0,0.707107,0.707107;3.14159rad)
  LinkedObject = -> Shape
  Placement = pos=(-111.125,28.575,5.5) rot=(0,0.707107,0.707107;3.14159rad)
FEATURE [App::Link] K_105_MX______________________________________1_______611CBFA4_2__ln_086  label="K_19_105_MX 轴标准键帽__¨¹_¡À__¡§1__¨¤_611DD897[2]"
  LinkPlacement = pos=(-120.125,38.075,9.5) rot=(1,0,0;1.5708rad)
  LinkedObject = -> Shape001
  Placement = pos=(-120.125,38.075,9.5) rot=(1,0,0;1.5708rad)
FEATURE [App::Link] K_105_cherry_mx_611CBFA4_ln_087  label="K_18_105_cherry mx_611DD882"
  LinkPlacement = pos=(-130.175,28.575,5.5) rot=(0,0.707107,0.707107;3.14159rad)
  LinkedObject = -> Shape
  Placement = pos=(-130.175,28.575,5.5) rot=(0,0.707107,0.707107;3.14159rad)
FEATURE [App::Link] K_105_MX______________________________________1_______611CBFA4_2__ln_087  label="K_18_105_MX 轴标准键帽__¨¹_¡À__¡§1__¨¤_611DD882[2]"
  LinkPlacement = pos=(-139.175,38.075,9.5) rot=(1,0,0;1.5708rad)
  LinkedObject = -> Shape001
  Placement = pos=(-139.175,38.075,9.5) rot=(1,0,0;1.5708rad)
FEATURE [App::Link] K_105_cherry_mx_611CBFA4_ln_088  label="K_17_105_cherry mx_611DD86D"
  LinkPlacement = pos=(136.525,28.575,5.5) rot=(0,0.707107,0.707107;3.14159rad)
  LinkedObject = -> Shape
  Placement = pos=(136.525,28.575,5.5) rot=(0,0.707107,0.707107;3.14159rad)
FEATURE [App::Link] K_105_MX______________________________________1_______611CBFA4_2__ln_088  label="K_17_105_MX 轴标准键帽__¨¹_¡À__¡§1__¨¤_611DD86D[2]"
  LinkPlacement = pos=(127.525,38.075,9.5) rot=(1,0,0;1.5708rad)
  LinkedObject = -> Shape001
  Placement = pos=(127.525,38.075,9.5) rot=(1,0,0;1.5708rad)
FEATURE [App::Link] K_105_cherry_mx_611CBFA4_ln_089  label="K_16_105_cherry mx_611DD858"
  LinkPlacement = pos=(117.475,47.625,5.5) rot=(0,0.707107,0.707107;3.14159rad)
  LinkedObject = -> Shape
  Placement = pos=(117.475,47.625,5.5) rot=(0,0.707107,0.707107;3.14159rad)
FEATURE [App::Link] K_105_MX______________________________________1_______611CBFA4_2__ln_089  label="K_16_105_MX 轴标准键帽__¨¹_¡À__¡§1__¨¤_611DD858[2]"
  LinkPlacement = pos=(108.475,57.125,9.5) rot=(1,0,0;1.5708rad)
  LinkedObject = -> Shape001
  Placement = pos=(108.475,57.125,9.5) rot=(1,0,0;1.5708rad)
FEATURE [App::Link] K_105_cherry_mx_611CBFA4_ln_090  label="K_15_105_cherry mx_611DD843"
  LinkPlacement = pos=(98.425,47.625,5.5) rot=(0,0.707107,0.707107;3.14159rad)
  LinkedObject = -> Shape
  Placement = pos=(98.425,47.625,5.5) rot=(0,0.707107,0.707107;3.14159rad)
FEATURE [App::Link] K_105_MX______________________________________1_______611CBFA4_2__ln_090  label="K_15_105_MX 轴标准键帽__¨¹_¡À__¡§1__¨¤_611DD843[2]"
  LinkPlacement = pos=(89.425,57.125,9.5) rot=(1,0,0;1.5708rad)
  LinkedObject = -> Shape001
  Placement = pos=(89.425,57.125,9.5) rot=(1,0,0;1.5708rad)
FEATURE [App::Link] K_105_cherry_mx_611CBFA4_ln_091  label="K_14_105_cherry mx_611DD82E"
  LinkPlacement = pos=(79.375,47.625,5.5) rot=(0,0.707107,0.707107;3.14159rad)
  LinkedObject = -> Shape
  Placement = pos=(79.375,47.625,5.5) rot=(0,0.707107,0.707107;3.14159rad)
FEATURE [App::Link] K_105_MX______________________________________1_______611CBFA4_2__ln_091  label="K_14_105_MX 轴标准键帽__¨¹_¡À__¡§1__¨¤_611DD82E[2]"
  LinkPlacement = pos=(70.375,57.125,9.5) rot=(1,0,0;1.5708rad)
  LinkedObject = -> Shape001
  Placement = pos=(70.375,57.125,9.5) rot=(1,0,0;1.5708rad)
FEATURE [App::Link] K_105_cherry_mx_611CBFA4_ln_092  label="K_13_105_cherry mx_611DD819"
  LinkPlacement = pos=(60.325,47.625,5.5) rot=(0,0.707107,0.707107;3.14159rad)
  LinkedObject = -> Shape
  Placement = pos=(60.325,47.625,5.5) rot=(0,0.707107,0.707107;3.14159rad)
FEATURE [App::Link] K_105_MX______________________________________1_______611CBFA4_2__ln_092  label="K_13_105_MX 轴标准键帽__¨¹_¡À__¡§1__¨¤_611DD819[2]"
  LinkPlacement = pos=(51.325,57.125,9.5) rot=(1,0,0;1.5708rad)
  LinkedObject = -> Shape001
  Placement = pos=(51.325,57.125,9.5) rot=(1,0,0;1.5708rad)
FEATURE [App::Link] K_105_cherry_mx_611CBFA4_ln_093  label="K_12_105_cherry mx_611DD804"
  LinkPlacement = pos=(41.275,47.625,5.5) rot=(0,0.707107,0.707107;3.14159rad)
  LinkedObject = -> Shape
  Placement = pos=(41.275,47.625,5.5) rot=(0,0.707107,0.707107;3.14159rad)
FEATURE [App::Link] K_105_MX______________________________________1_______611CBFA4_2__ln_093  label="K_12_105_MX 轴标准键帽__¨¹_¡À__¡§1__¨¤_611DD804[2]"
  LinkPlacement = pos=(32.275,57.125,9.5) rot=(1,0,0;1.5708rad)
  LinkedObject = -> Shape001
  Placement = pos=(32.275,57.125,9.5) rot=(1,0,0;1.5708rad)
FEATURE [App::Link] K_105_cherry_mx_611CBFA4_ln_094  label="K_11_105_cherry mx_611DD7EF"
  LinkPlacement = pos=(22.225,47.625,5.5) rot=(0,0.707107,0.707107;3.14159rad)
  LinkedObject = -> Shape
  Placement = pos=(22.225,47.625,5.5) rot=(0,0.707107,0.707107;3.14159rad)
FEATURE [App::Link] K_105_MX______________________________________1_______611CBFA4_2__ln_094  label="K_11_105_MX 轴标准键帽__¨¹_¡À__¡§1__¨¤_611DD7EF[2]"
  LinkPlacement = pos=(13.225,57.125,9.5) rot=(1,0,0;1.5708rad)
  LinkedObject = -> Shape001
  Placement = pos=(13.225,57.125,9.5) rot=(1,0,0;1.5708rad)
FEATURE [App::Link] K_105_cherry_mx_611CBFA4_ln_095  label="K_10_105_cherry mx_611DD7DA"
  LinkPlacement = pos=(3.175,47.625,5.5) rot=(0,0.707107,0.707107;3.14159rad)
  LinkedObject = -> Shape
  Placement = pos=(3.175,47.625,5.5) rot=(0,0.707107,0.707107;3.14159rad)
FEATURE [App::Link] K_105_MX______________________________________1_______611CBFA4_2__ln_095  label="K_10_105_MX 轴标准键帽__¨¹_¡À__¡§1__¨¤_611DD7DA[2]"
  LinkPlacement = pos=(-5.825,57.125,9.5) rot=(1,0,0;1.5708rad)
  LinkedObject = -> Shape001
  Placement = pos=(-5.825,57.125,9.5) rot=(1,0,0;1.5708rad)
FEATURE [App::Link] K_105_cherry_mx_611CBFA4_ln_096  label="K_104_105_cherry mx_611CBF8B"
  LinkPlacement = pos=(79.375,-47.6255,5.5) rot=(0,0.707107,0.707107;3.14159rad)
  LinkedObject = -> Shape
  Placement = pos=(79.375,-47.6255,5.5) rot=(0,0.707107,0.707107;3.14159rad)
FEATURE [App::Link] K_105_cherry_mx_611CBFA4_ln_097  label="K_96_105_cherry mx_611CBF76"
  LinkPlacement = pos=(-73.025,-47.6255,5.5) rot=(0,0.707107,0.707107;3.14159rad)
  LinkedObject = -> Shape
  Placement = pos=(-73.025,-47.6255,5.5) rot=(0,0.707107,0.707107;3.14159rad)
FEATURE [Part::Feature] Part__Feature  label="mx Stabilizer base 16828"
  shape: bbox 6.802 x 10.1 x 19.67 mm, 163 faces (baked)
FEATURE [Part::Feature] Part__Feature001  label="mx Stabilizer key 16828"
  Placement = pos=(0,8.1,0) rot=(0,0,1;0rad)
  shape: bbox 4.6 x 11.96 x 8.302 mm, 299 faces (baked)
FEATURE [Part::Feature] Part__Feature002  label="metal stick 16828"
  Placement = pos=(11.95,4.09188,-1.57187) rot=(1,0,0;0.574181rad)
  shape: bbox 25.8 x 7.719 x 10.9 mm, 12 faces (baked)
FEATURE [Part::Feature] Part__Feature003  label="mx Stabilizer base 16829"
  Placement = pos=(23.9,-1.1e-15,-2e-16) rot=(0,0,1;0rad)
  shape: bbox 6.802 x 10.1 x 19.67 mm, 163 faces (baked)
FEATURE [Part::Feature] Part__Feature004  label="mx Stabilizer key 16829"
  Placement = pos=(23.9,8.1,0) rot=(0,0,1;0rad)
  shape: bbox 4.6 x 11.96 x 8.302 mm, 299 faces (baked)
FEATURE [App::Part] Stabilizer___open  label="K_89_Stabilizer - open_611CBF5D"
  Group = -> [Part__Feature,Part__Feature001,Part__Feature002,Part__Feature003,Part__Feature004]
  Origin = -> Origin008
  Placement = pos=(134.05,-28.5755,3.5) rot=(1,0,0;1.5708rad)
FEATURE [App::Link] K_105_cherry_mx_611CBFA4_ln_098  label="K_89_105_cherry mx_611CBF5D[2]"
  LinkPlacement = pos=(146.05,-28.5755,5.5) rot=(0,0.707107,0.707107;3.14159rad)
  LinkedObject = -> Shape
  Placement = pos=(146.05,-28.5755,5.5) rot=(0,0.707107,0.707107;3.14159rad)
FEATURE [App::Link] K_89_Stabilizer___open_611CBF5D_ln_  label="K_74_89_Stabilizer - open_611CBF44"
  LinkPlacement = pos=(-151.7,-28.5755,3.5) rot=(1,0,0;1.5708rad)
  LinkedObject = -> Stabilizer___open
  Placement = pos=(-151.7,-28.5755,3.5) rot=(1,0,0;1.5708rad)
FEATURE [App::Link] K_105_cherry_mx_611CBFA4_ln_099  label="K_74_105_cherry mx_611CBF44[2]"
  LinkPlacement = pos=(-139.7,-28.5755,5.5) rot=(0,0.707107,0.707107;3.14159rad)
  LinkedObject = -> Shape
  Placement = pos=(-139.7,-28.5755,5.5) rot=(0,0.707107,0.707107;3.14159rad)
FEATURE [App::Link] K_89_Stabilizer___open_611CBF5D_ln_001  label="K_70_89_Stabilizer - open_611CBF2B"
  LinkPlacement = pos=(134.05,-9.525,3.5) rot=(1,0,0;1.5708rad)
  LinkedObject = -> Stabilizer___open
  Placement = pos=(134.05,-9.525,3.5) rot=(1,0,0;1.5708rad)
FEATURE [App::Link] K_105_cherry_mx_611CBFA4_ln_100  label="K_70_105_cherry mx_611CBF2B[2]"
  LinkPlacement = pos=(146.05,-9.525,5.5) rot=(0,0.707107,0.707107;3.14159rad)
  LinkedObject = -> Shape
  Placement = pos=(146.05,-9.525,5.5) rot=(0,0.707107,0.707107;3.14159rad)
FEATURE [App::Link] K_89_Stabilizer___open_611CBF5D_ln_002  label="K_55_89_Stabilizer - open_611CBF12"
  LinkPlacement = pos=(-151.7,-9.525,3.5) rot=(1,0,0;1.5708rad)
  LinkedObject = -> Stabilizer___open
  Placement = pos=(-151.7,-9.525,3.5) rot=(1,0,0;1.5708rad)
FEATURE [App::Link] K_105_cherry_mx_611CBFA4_ln_101  label="K_55_105_cherry mx_611CBF12[2]"
  LinkPlacement = pos=(-139.7,-9.525,5.5) rot=(0,0.707107,0.707107;3.14159rad)
  LinkedObject = -> Shape
  Placement = pos=(-139.7,-9.525,5.5) rot=(0,0.707107,0.707107;3.14159rad)
FEATURE [App::Link] K_89_Stabilizer___open_611CBF5D_ln_003  label="K_36_89_Stabilizer - open_611CBEF9"
  LinkPlacement = pos=(-151.7,9.525,3.5) rot=(1,0,0;1.5708rad)
  LinkedObject = -> Stabilizer___open
  Placement = pos=(-151.7,9.525,3.5) rot=(1,0,0;1.5708rad)
FEATURE [App::Link] K_105_cherry_mx_611CBFA4_ln_102  label="K_36_105_cherry mx_611CBEF9[2]"
  LinkPlacement = pos=(-139.7,9.525,5.5) rot=(0,0.707107,0.707107;3.14159rad)
  LinkedObject = -> Shape
  Placement = pos=(-139.7,9.525,5.5) rot=(0,0.707107,0.707107;3.14159rad)
FEATURE [App::Link] K_89_Stabilizer___open_611CBF5D_ln_004  label="K_32_89_Stabilizer - open_611CBEE0"
  LinkPlacement = pos=(115,28.575,3.5) rot=(1,0,0;1.5708rad)
  LinkedObject = -> Stabilizer___open
  Placement = pos=(115,28.575,3.5) rot=(1,0,0;1.5708rad)
FEATURE [App::Link] K_105_cherry_mx_611CBFA4_ln_103  label="K_32_105_cherry mx_611CBEE0[2]"
  LinkPlacement = pos=(127,28.575,5.5) rot=(0,0.707107,0.707107;3.14159rad)
  LinkedObject = -> Shape
  Placement = pos=(127,28.575,5.5) rot=(0,0.707107,0.707107;3.14159rad)
FEATURE [Part::Feature] Part__Feature005  label="SHELL"
  shape: bbox 2.5 x 2.5 x 0.6 mm, 1 faces, 0 solids (baked)
FEATURE [Part::Feature] Part__Feature006  label="SOLID"
  shape: bbox 5.88 x 2.8 x 1.6 mm, 77 faces (baked)
FEATURE [App::Part] _228_reverse_mount_led_v1  label="D24_3228_reverse_mount_led v1_611CB79E[2]"
  Group = -> [Part__Feature005,Part__Feature006]
  Origin = -> Origin009
  Placement = pos=(108.418,-42.1405,-1.5) rot=(0,0,1;1.5708rad)
FEATURE [App::Link] D24_3228_reverse_mount_led_v1_611CB79E_2__ln_  label="D23_3228_reverse_mount_led v1_611CB784[2]"
  LinkPlacement = pos=(51.307,-42.3555,-1.5) rot=(0,0,1;1.5708rad)
  LinkedObject = -> _228_reverse_mount_led_v1
  Placement = pos=(51.307,-42.3555,-1.5) rot=(0,0,1;1.5708rad)
FEATURE [App::Link] D24_3228_reverse_mount_led_v1_611CB79E_2__ln_001  label="D22_3228_reverse_mount_led v1_611CB76A[2]"
  LinkPlacement = pos=(-62.904,-42.1405,-1.5) rot=(0,0,1;1.5708rad)
  LinkedObject = -> _228_reverse_mount_led_v1
  Placement = pos=(-62.904,-42.1405,-1.5) rot=(0,0,1;1.5708rad)
FEATURE [App::Link] D24_3228_reverse_mount_led_v1_611CB79E_2__ln_002  label="D21_3228_reverse_mount_led v1_611CB750[2]"
  LinkPlacement = pos=(-120.245,-42.3935,-1.5) rot=(0,0,1;1.5708rad)
  LinkedObject = -> _228_reverse_mount_led_v1
  Placement = pos=(-120.245,-42.3935,-1.5) rot=(0,0,1;1.5708rad)
FEATURE [Part::Feature] Shape002  label="R7_R_0603_1608Metric_611CC01B"
  Placement = pos=(-146.018,21.2407,-1.6) rot=(0,1,0;3.14159rad)
  shape: bbox 1.6 x 0.8 x 0.45 mm, 26 faces (baked)
FEATURE [App::Link] R7_R_0603_1608Metric_611CC01B_ln_  label="R7_R_0603_1608Metric_611CC01B[2]"
  LinkPlacement = pos=(-146.018,21.2407,-1.6) rot=(0,1,0;3.14159rad)
  LinkedObject = -> Shape002
  Placement = pos=(-146.018,21.2407,-1.6) rot=(0,1,0;3.14159rad)
FEATURE [App::Link] R7_R_0603_1608Metric_611CC01B_ln_001  label="R6_R_0603_1608Metric_611CC011"
  LinkPlacement = pos=(-158.178,36.5125,-1.6) rot=(0.707107,0.707107,0;3.14159rad)
  LinkedObject = -> Shape002
  Placement = pos=(-158.178,36.5125,-1.6) rot=(0.707107,0.707107,0;3.14159rad)
FEATURE [App::Link] R7_R_0603_1608Metric_611CC01B_ln_002  label="R6_R_0603_1608Metric_611CC011[2]"
  LinkPlacement = pos=(-158.178,36.5125,-1.6) rot=(0.707107,0.707107,0;3.14159rad)
  LinkedObject = -> Shape002
  Placement = pos=(-158.178,36.5125,-1.6) rot=(0.707107,0.707107,0;3.14159rad)
FEATURE [App::Link] R7_R_0603_1608Metric_611CC01B_ln_003  label="R4_R_0603_1608Metric_611CBFF6"
  LinkPlacement = pos=(-155.257,22.1933,-1.6) rot=(1,0,0;3.14159rad)
  LinkedObject = -> Shape002
  Placement = pos=(-155.257,22.1933,-1.6) rot=(1,0,0;3.14159rad)
FEATURE [App::Link] R7_R_0603_1608Metric_611CC01B_ln_004  label="R4_R_0603_1608Metric_611CBFF6[2]"
  LinkPlacement = pos=(-155.257,22.1933,-1.6) rot=(1,0,0;3.14159rad)
  LinkedObject = -> Shape002
  Placement = pos=(-155.257,22.1933,-1.6) rot=(1,0,0;3.14159rad)
FEATURE [App::Link] R7_R_0603_1608Metric_611CC01B_ln_005  label="R3_R_0603_1608Metric_611CBFEC"
  LinkPlacement = pos=(-155.257,23.7807,-1.6) rot=(0,1,0;3.14159rad)
  LinkedObject = -> Shape002
  Placement = pos=(-155.257,23.7807,-1.6) rot=(0,1,0;3.14159rad)
FEATURE [App::Link] R7_R_0603_1608Metric_611CC01B_ln_006  label="R3_R_0603_1608Metric_611CBFEC[2]"
  LinkPlacement = pos=(-155.257,23.7807,-1.6) rot=(0,1,0;3.14159rad)
  LinkedObject = -> Shape002
  Placement = pos=(-155.257,23.7807,-1.6) rot=(0,1,0;3.14159rad)
FEATURE [App::Link] R7_R_0603_1608Metric_611CC01B_ln_007  label="R2_R_0603_1608Metric_611CBFE2"
  LinkPlacement = pos=(-95.758,38.0365,-1.6) rot=(-0.707107,0.707107,0;3.14159rad)
  LinkedObject = -> Shape002
  Placement = pos=(-95.758,38.0365,-1.6) rot=(-0.707107,0.707107,0;3.14159rad)
FEATURE [App::Link] R7_R_0603_1608Metric_611CC01B_ln_008  label="R2_R_0603_1608Metric_611CBFE2[2]"
  LinkPlacement = pos=(-95.758,38.0365,-1.6) rot=(-0.707107,0.707107,0;3.14159rad)
  LinkedObject = -> Shape002
  Placement = pos=(-95.758,38.0365,-1.6) rot=(-0.707107,0.707107,0;3.14159rad)
FEATURE [App::Link] R7_R_0603_1608Metric_611CC01B_ln_009  label="R1_R_0603_1608Metric_611CBFD8"
  LinkPlacement = pos=(-98.425,35.3695,-1.6) rot=(0,1,0;3.14159rad)
  LinkedObject = -> Shape002
  Placement = pos=(-98.425,35.3695,-1.6) rot=(0,1,0;3.14159rad)
FEATURE [App::Link] R7_R_0603_1608Metric_611CC01B_ln_010  label="R1_R_0603_1608Metric_611CBFD8[2]"
  LinkPlacement = pos=(-98.425,35.3695,-1.6) rot=(0,1,0;3.14159rad)
  LinkedObject = -> Shape002
  Placement = pos=(-98.425,35.3695,-1.6) rot=(0,1,0;3.14159rad)
FEATURE [Part::Feature] Shape003  label="C37_C_0603_1608Metric_611CB56A"
  Placement = pos=(109.156,-46.4185,-1.6) rot=(0.707107,0.707107,0;3.14159rad)
  shape: bbox 0.8 x 1.6 x 0.8 mm, 28 faces (baked)
FEATURE [App::Link] C37_C_0603_1608Metric_611CB56A_ln_  label="C36_C_0603_1608Metric_611CB560"
  LinkPlacement = pos=(52.045,-46.6345,-1.6) rot=(0.707107,0.707107,0;3.14159rad)
  LinkedObject = -> Shape003
  Placement = pos=(52.045,-46.6345,-1.6) rot=(0.707107,0.707107,0;3.14159rad)
FEATURE [App::Link] C37_C_0603_1608Metric_611CB56A_ln_001  label="C35_C_0603_1608Metric_611CB556"
  LinkPlacement = pos=(-62.166,-46.2285,-1.6) rot=(0.707107,0.707107,0;3.14159rad)
  LinkedObject = -> Shape003
  Placement = pos=(-62.166,-46.2285,-1.6) rot=(0.707107,0.707107,0;3.14159rad)
FEATURE [App::Link] C37_C_0603_1608Metric_611CB56A_ln_002  label="C34_C_0603_1608Metric_611CB54C"
  LinkPlacement = pos=(-119.507,-46.5455,-1.6) rot=(0.707107,0.707107,0;3.14159rad)
  LinkedObject = -> Shape003
  Placement = pos=(-119.507,-46.5455,-1.6) rot=(0.707107,0.707107,0;3.14159rad)
FEATURE [App::Link] C37_C_0603_1608Metric_611CB56A_ln_003  label="C33_C_0603_1608Metric_611CB542"
  LinkPlacement = pos=(-99.568,-34.3535,-1.6) rot=(1,0,0;3.14159rad)
  LinkedObject = -> Shape003
  Placement = pos=(-99.568,-34.3535,-1.6) rot=(1,0,0;3.14159rad)
FEATURE [App::Link] C37_C_0603_1608Metric_611CB56A_ln_004  label="C32_C_0603_1608Metric_611CB538"
  LinkPlacement = pos=(-42.545,-34.3535,-1.6) rot=(1,0,0;3.14159rad)
  LinkedObject = -> Shape003
  Placement = pos=(-42.545,-34.3535,-1.6) rot=(1,0,0;3.14159rad)
FEATURE [App::Link] C37_C_0603_1608Metric_611CB56A_ln_005  label="C31_C_0603_1608Metric_611CB52E"
  LinkPlacement = pos=(5.08,-34.3535,-1.6) rot=(1,0,0;3.14159rad)
  LinkedObject = -> Shape003
  Placement = pos=(5.08,-34.3535,-1.6) rot=(1,0,0;3.14159rad)
FEATURE [App::Link] C37_C_0603_1608Metric_611CB56A_ln_006  label="C30_C_0603_1608Metric_611CB524"
  LinkPlacement = pos=(71.704,-34.3785,-1.6) rot=(1,0,0;3.14159rad)
  LinkedObject = -> Shape003
  Placement = pos=(71.704,-34.3785,-1.6) rot=(1,0,0;3.14159rad)
FEATURE [App::Link] C37_C_0603_1608Metric_611CB56A_ln_007  label="C29_C_0603_1608Metric_611CB51A"
  LinkPlacement = pos=(129.032,-34.3535,-1.6) rot=(1,0,0;3.14159rad)
  LinkedObject = -> Shape003
  Placement = pos=(129.032,-34.3535,-1.6) rot=(1,0,0;3.14159rad)
FEATURE [App::Link] C37_C_0603_1608Metric_611CB56A_ln_008  label="C28_C_0603_1608Metric_611CB510"
  LinkPlacement = pos=(128.905,-15.3035,-1.6) rot=(1,0,0;3.14159rad)
  LinkedObject = -> Shape003
  Placement = pos=(128.905,-15.3035,-1.6) rot=(1,0,0;3.14159rad)
FEATURE [App::Link] C37_C_0603_1608Metric_611CB56A_ln_009  label="C27_C_0603_1608Metric_611CB506"
  LinkPlacement = pos=(71.882,-15.3035,-1.6) rot=(1,0,0;3.14159rad)
  LinkedObject = -> Shape003
  Placement = pos=(71.882,-15.3035,-1.6) rot=(1,0,0;3.14159rad)
FEATURE [App::Link] C37_C_0603_1608Metric_611CB56A_ln_010  label="C26_C_0603_1608Metric_611CB4FC"
  LinkPlacement = pos=(5.08,-15.3035,-1.6) rot=(1,0,0;3.14159rad)
  LinkedObject = -> Shape003
  Placement = pos=(5.08,-15.3035,-1.6) rot=(1,0,0;3.14159rad)
FEATURE [App::Link] C37_C_0603_1608Metric_611CB56A_ln_011  label="C25_C_0603_1608Metric_611CB4F2"
  LinkPlacement = pos=(-42.545,-15.3035,-1.6) rot=(1,0,0;3.14159rad)
  LinkedObject = -> Shape003
  Placement = pos=(-42.545,-15.3035,-1.6) rot=(1,0,0;3.14159rad)
FEATURE [App::Link] C37_C_0603_1608Metric_611CB56A_ln_012  label="C24_C_0603_1608Metric_611CB4E8"
  LinkPlacement = pos=(-99.695,-15.3035,-1.6) rot=(1,0,0;3.14159rad)
  LinkedObject = -> Shape003
  Placement = pos=(-99.695,-15.3035,-1.6) rot=(1,0,0;3.14159rad)
FEATURE [App::Link] C37_C_0603_1608Metric_611CB56A_ln_013  label="C23_C_0603_1608Metric_611CB4DE"
  LinkPlacement = pos=(-99.695,3.7465,-1.6) rot=(1,0,0;3.14159rad)
  LinkedObject = -> Shape003
  Placement = pos=(-99.695,3.7465,-1.6) rot=(1,0,0;3.14159rad)
FEATURE [App::Link] C37_C_0603_1608Metric_611CB56A_ln_014  label="C22_C_0603_1608Metric_611CB4D4"
  LinkPlacement = pos=(-42.545,3.7465,-1.6) rot=(1,0,0;3.14159rad)
  LinkedObject = -> Shape003
  Placement = pos=(-42.545,3.7465,-1.6) rot=(1,0,0;3.14159rad)
FEATURE [App::Link] C37_C_0603_1608Metric_611CB56A_ln_015  label="C21_C_0603_1608Metric_611CB4CA"
  LinkPlacement = pos=(5.08,3.7465,-1.6) rot=(1,0,0;3.14159rad)
  LinkedObject = -> Shape003
  Placement = pos=(5.08,3.7465,-1.6) rot=(1,0,0;3.14159rad)
FEATURE [App::Link] C37_C_0603_1608Metric_611CB56A_ln_016  label="C20_C_0603_1608Metric_611CB4C0"
  LinkPlacement = pos=(71.755,3.7465,-1.6) rot=(1,0,0;3.14159rad)
  LinkedObject = -> Shape003
  Placement = pos=(71.755,3.7465,-1.6) rot=(1,0,0;3.14159rad)
FEATURE [App::Link] C37_C_0603_1608Metric_611CB56A_ln_017  label="C19_C_0603_1608Metric_611CB4B6"
  LinkPlacement = pos=(128.778,3.7465,-1.6) rot=(1,0,0;3.14159rad)
  LinkedObject = -> Shape003
  Placement = pos=(128.778,3.7465,-1.6) rot=(1,0,0;3.14159rad)
FEATURE [App::Link] C37_C_0603_1608Metric_611CB56A_ln_018  label="C18_C_0603_1608Metric_611CB4AC"
  LinkPlacement = pos=(128.905,22.7965,-1.6) rot=(1,0,0;3.14159rad)
  LinkedObject = -> Shape003
  Placement = pos=(128.905,22.7965,-1.6) rot=(1,0,0;3.14159rad)
FEATURE [App::Link] C37_C_0603_1608Metric_611CB56A_ln_019  label="C17_C_0603_1608Metric_611CB4A2"
  LinkPlacement = pos=(71.628,22.7965,-1.6) rot=(1,0,0;3.14159rad)
  LinkedObject = -> Shape003
  Placement = pos=(71.628,22.7965,-1.6) rot=(1,0,0;3.14159rad)
FEATURE [App::Link] C37_C_0603_1608Metric_611CB56A_ln_020  label="C16_C_0603_1608Metric_611CB498"
  LinkPlacement = pos=(5.08,22.7965,-1.6) rot=(1,0,0;3.14159rad)
  LinkedObject = -> Shape003
  Placement = pos=(5.08,22.7965,-1.6) rot=(1,0,0;3.14159rad)
FEATURE [App::Link] C37_C_0603_1608Metric_611CB56A_ln_021  label="C15_C_0603_1608Metric_611CB48E"
  LinkPlacement = pos=(-42.672,22.7965,-1.6) rot=(1,0,0;3.14159rad)
  LinkedObject = -> Shape003
  Placement = pos=(-42.672,22.7965,-1.6) rot=(1,0,0;3.14159rad)
FEATURE [App::Link] C37_C_0603_1608Metric_611CB56A_ln_022  label="C14_C_0603_1608Metric_611CB484"
  LinkPlacement = pos=(-99.695,22.9235,-1.6) rot=(1,0,0;3.14159rad)
  LinkedObject = -> Shape003
  Placement = pos=(-99.695,22.9235,-1.6) rot=(1,0,0;3.14159rad)
FEATURE [App::Link] C37_C_0603_1608Metric_611CB56A_ln_023  label="C13_C_0603_1608Metric_611CB47A"
  LinkPlacement = pos=(-145.962,22.8283,-1.6) rot=(0,1,0;3.14159rad)
  LinkedObject = -> Shape003
  Placement = pos=(-145.962,22.8283,-1.6) rot=(0,1,0;3.14159rad)
FEATURE [App::Link] C37_C_0603_1608Metric_611CB56A_ln_024  label="C12_C_0603_1608Metric_611CB470"
  LinkPlacement = pos=(-140.875,26.5113,-1.6) rot=(-0.707107,0.707107,0;3.14159rad)
  LinkedObject = -> Shape003
  Placement = pos=(-140.875,26.5113,-1.6) rot=(-0.707107,0.707107,0;3.14159rad)
FEATURE [App::Link] C37_C_0603_1608Metric_611CB56A_ln_025  label="C11_C_0603_1608Metric_611CB466"
  LinkPlacement = pos=(-51.054,4.7625,-1.6) rot=(1,0,0;3.14159rad)
  LinkedObject = -> Shape003
  Placement = pos=(-51.054,4.7625,-1.6) rot=(1,0,0;3.14159rad)
FEATURE [App::Link] C37_C_0603_1608Metric_611CB56A_ln_026  label="C10_C_0603_1608Metric_611CB45C"
  LinkPlacement = pos=(-50.165,-1.0795,-1.6) rot=(1,0,0;3.14159rad)
  LinkedObject = -> Shape003
  Placement = pos=(-50.165,-1.0795,-1.6) rot=(1,0,0;3.14159rad)
FEATURE [App::Link] C37_C_0603_1608Metric_611CB56A_ln_027  label="C9_C_0603_1608Metric_611CB452"
  LinkPlacement = pos=(-79.375,19.05,-1.6) rot=(-0.707107,0.707107,0;3.14159rad)
  LinkedObject = -> Shape003
  Placement = pos=(-79.375,19.05,-1.6) rot=(-0.707107,0.707107,0;3.14159rad)
FEATURE [App::Link] C37_C_0603_1608Metric_611CB56A_ln_028  label="C8_C_0603_1608Metric_611CB448"
  LinkPlacement = pos=(-85.725,19.05,-1.6) rot=(-0.707107,0.707107,0;3.14159rad)
  LinkedObject = -> Shape003
  Placement = pos=(-85.725,19.05,-1.6) rot=(-0.707107,0.707107,0;3.14159rad)
FEATURE [App::Link] C37_C_0603_1608Metric_611CB56A_ln_029  label="C7_C_0603_1608Metric_611CB43E"
  LinkPlacement = pos=(-154.464,33.6233,-1.6) rot=(-0.707107,0.707107,0;3.14159rad)
  LinkedObject = -> Shape003
  Placement = pos=(-154.464,33.6233,-1.6) rot=(-0.707107,0.707107,0;3.14159rad)
FEATURE [App::Link] C37_C_0603_1608Metric_611CB56A_ln_030  label="C6_C_0603_1608Metric_611CB434"
  LinkPlacement = pos=(-61.722,-8.1915,-1.6) rot=(0.707107,0.707107,0;3.14159rad)
  LinkedObject = -> Shape003
  Placement = pos=(-61.722,-8.1915,-1.6) rot=(0.707107,0.707107,0;3.14159rad)
FEATURE [App::Link] C37_C_0603_1608Metric_611CB56A_ln_031  label="C5_C_0603_1608Metric_611CB42A"
  LinkPlacement = pos=(-55.88,-3.6195,-1.6) rot=(0.707107,0.707107,0;3.14159rad)
  LinkedObject = -> Shape003
  Placement = pos=(-55.88,-3.6195,-1.6) rot=(0.707107,0.707107,0;3.14159rad)
FEATURE [App::Link] C37_C_0603_1608Metric_611CB56A_ln_032  label="C4_C_0603_1608Metric_611CB420"
  LinkPlacement = pos=(-65.532,-8.0645,-1.6) rot=(0.707107,0.707107,0;3.14159rad)
  LinkedObject = -> Shape003
  Placement = pos=(-65.532,-8.0645,-1.6) rot=(0.707107,0.707107,0;3.14159rad)
FEATURE [App::Link] C37_C_0603_1608Metric_611CB56A_ln_033  label="C3_C_0603_1608Metric_611CB416"
  LinkPlacement = pos=(-73.279,5.0165,-1.6) rot=(1,0,0;3.14159rad)
  LinkedObject = -> Shape003
  Placement = pos=(-73.279,5.0165,-1.6) rot=(1,0,0;3.14159rad)
FEATURE [App::Link] C37_C_0603_1608Metric_611CB56A_ln_034  label="C2_C_0603_1608Metric_611CB40C"
  LinkPlacement = pos=(-62.23,10.8585,-1.6) rot=(-0.707107,0.707107,0;3.14159rad)
  LinkedObject = -> Shape003
  Placement = pos=(-62.23,10.8585,-1.6) rot=(-0.707107,0.707107,0;3.14159rad)
FEATURE [App::Link] C37_C_0603_1608Metric_611CB56A_ln_035  label="C1_C_0603_1608Metric_611CB402"
  LinkPlacement = pos=(-75.819,4.1275,-1.6) rot=(-0.707107,0.707107,0;3.14159rad)
  LinkedObject = -> Shape003
  Placement = pos=(-75.819,4.1275,-1.6) rot=(-0.707107,0.707107,0;3.14159rad)
FEATURE [Part::Feature] Shape004  label="D_2_D_SOD_123_611CB7E4"
  Placement = pos=(-122.174,47.3075,-1.6) rot=(0.707107,0.707107,0;3.14159rad)
  shape: bbox 1.6 x 3.8 x 1.25 mm, 67 faces (baked)
FEATURE [App::Link] D_2_D_SOD_123_611CB7E4_ln_  label="D_1_2_D_SOD_123_611CB7D3"
  LinkPlacement = pos=(-141.224,47.3085,-1.6) rot=(0.707107,0.707107,0;3.14159rad)
  LinkedObject = -> Shape004
  Placement = pos=(-141.224,47.3085,-1.6) rot=(0.707107,0.707107,0;3.14159rad)
FEATURE [App::Link] D_2_D_SOD_123_611CB7E4_ln_001  label="D_100_2_D_SOD_123_611CBE66"
  LinkPlacement = pos=(147.637,-47.2435,-1.6) rot=(0.707107,0.707107,0;3.14159rad)
  LinkedObject = -> Shape004
  Placement = pos=(147.637,-47.2435,-1.6) rot=(0.707107,0.707107,0;3.14159rad)
FEATURE [App::Link] D_2_D_SOD_123_611CB7E4_ln_002  label="D_99_2_D_SOD_123_611CBE55"
  LinkPlacement = pos=(144.463,-47.2435,-1.6) rot=(0.707107,0.707107,0;3.14159rad)
  LinkedObject = -> Shape004
  Placement = pos=(144.463,-47.2435,-1.6) rot=(0.707107,0.707107,0;3.14159rad)
FEATURE [App::Link] D_2_D_SOD_123_611CB7E4_ln_003  label="D_98_2_D_SOD_123_611CBE44"
  LinkPlacement = pos=(125.476,-47.2435,-1.6) rot=(0.707107,0.707107,0;3.14159rad)
  LinkedObject = -> Shape004
  Placement = pos=(125.476,-47.2435,-1.6) rot=(0.707107,0.707107,0;3.14159rad)
FEATURE [App::Link] D_2_D_SOD_123_611CB7E4_ln_004  label="D_97_2_D_SOD_123_611CBE33"
  LinkPlacement = pos=(106.363,-47.2435,-1.6) rot=(0.707107,0.707107,0;3.14159rad)
  LinkedObject = -> Shape004
  Placement = pos=(106.363,-47.2435,-1.6) rot=(0.707107,0.707107,0;3.14159rad)
FEATURE [App::Link] D_2_D_SOD_123_611CB7E4_ln_005  label="D_96_2_D_SOD_123_611CBE22"
  LinkPlacement = pos=(87.313,-47.2435,-1.6) rot=(0.707107,0.707107,0;3.14159rad)
  LinkedObject = -> Shape004
  Placement = pos=(87.313,-47.2435,-1.6) rot=(0.707107,0.707107,0;3.14159rad)
FEATURE [App::Link] D_2_D_SOD_123_611CB7E4_ln_006  label="D_95_2_D_SOD_123_611CBE11"
  LinkPlacement = pos=(68.326,-47.2435,-1.6) rot=(0.707107,0.707107,0;3.14159rad)
  LinkedObject = -> Shape004
  Placement = pos=(68.326,-47.2435,-1.6) rot=(0.707107,0.707107,0;3.14159rad)
FEATURE [App::Link] D_2_D_SOD_123_611CB7E4_ln_007  label="D_94_2_D_SOD_123_611CBE00"
  LinkPlacement = pos=(49.213,-47.2435,-1.6) rot=(0.707107,0.707107,0;3.14159rad)
  LinkedObject = -> Shape004
  Placement = pos=(49.213,-47.2435,-1.6) rot=(0.707107,0.707107,0;3.14159rad)
FEATURE [App::Link] D_2_D_SOD_123_611CB7E4_ln_008  label="D_93_2_D_SOD_123_611CBDEF"
  LinkPlacement = pos=(30.163,-47.2435,-1.6) rot=(0.707107,0.707107,0;3.14159rad)
  LinkedObject = -> Shape004
  Placement = pos=(30.163,-47.2435,-1.6) rot=(0.707107,0.707107,0;3.14159rad)
FEATURE [App::Link] D_2_D_SOD_123_611CB7E4_ln_009  label="D_92_2_D_SOD_123_611CBDDE"
  LinkPlacement = pos=(11.176,-47.2435,-1.6) rot=(0.707107,0.707107,0;3.14159rad)
  LinkedObject = -> Shape004
  Placement = pos=(11.176,-47.2435,-1.6) rot=(0.707107,0.707107,0;3.14159rad)
FEATURE [App::Link] D_2_D_SOD_123_611CB7E4_ln_010  label="D_91_2_D_SOD_123_611CBDCD"
  LinkPlacement = pos=(-7.874,-47.2435,-1.6) rot=(0.707107,0.707107,0;3.14159rad)
  LinkedObject = -> Shape004
  Placement = pos=(-7.874,-47.2435,-1.6) rot=(0.707107,0.707107,0;3.14159rad)
FEATURE [App::Link] D_2_D_SOD_123_611CB7E4_ln_011  label="D_90_2_D_SOD_123_611CBDBC"
  LinkPlacement = pos=(-26.987,-47.3075,-1.6) rot=(0.707107,0.707107,0;3.14159rad)
  LinkedObject = -> Shape004
  Placement = pos=(-26.987,-47.3075,-1.6) rot=(0.707107,0.707107,0;3.14159rad)
FEATURE [App::Link] D_2_D_SOD_123_611CB7E4_ln_012  label="D_89_2_D_SOD_123_611CBDAB"
  LinkPlacement = pos=(-46.037,-47.2435,-1.6) rot=(0.707107,0.707107,0;3.14159rad)
  LinkedObject = -> Shape004
  Placement = pos=(-46.037,-47.2435,-1.6) rot=(0.707107,0.707107,0;3.14159rad)
FEATURE [App::Link] D_2_D_SOD_123_611CB7E4_ln_013  label="D_88_2_D_SOD_123_611CBD9A"
  LinkPlacement = pos=(-65.087,-47.2435,-1.6) rot=(0.707107,0.707107,0;3.14159rad)
  LinkedObject = -> Shape004
  Placement = pos=(-65.087,-47.2435,-1.6) rot=(0.707107,0.707107,0;3.14159rad)
FEATURE [App::Link] D_2_D_SOD_123_611CB7E4_ln_014  label="D_87_2_D_SOD_123_611CBD89"
  LinkPlacement = pos=(-84.1375,-47.3075,-1.6) rot=(0.707107,0.707107,0;3.14159rad)
  LinkedObject = -> Shape004
  Placement = pos=(-84.1375,-47.3075,-1.6) rot=(0.707107,0.707107,0;3.14159rad)
FEATURE [App::Link] D_2_D_SOD_123_611CB7E4_ln_015  label="D_86_2_D_SOD_123_611CBD78"
  LinkPlacement = pos=(-103.187,-47.2435,-1.6) rot=(0.707107,0.707107,0;3.14159rad)
  LinkedObject = -> Shape004
  Placement = pos=(-103.187,-47.2435,-1.6) rot=(0.707107,0.707107,0;3.14159rad)
FEATURE [App::Link] D_2_D_SOD_123_611CB7E4_ln_016  label="D_85_2_D_SOD_123_611CBD67"
  LinkPlacement = pos=(-122.237,-47.3075,-1.6) rot=(0.707107,0.707107,0;3.14159rad)
  LinkedObject = -> Shape004
  Placement = pos=(-122.237,-47.3075,-1.6) rot=(0.707107,0.707107,0;3.14159rad)
FEATURE [App::Link] D_2_D_SOD_123_611CB7E4_ln_017  label="D_84_2_D_SOD_123_611CBD56"
  LinkPlacement = pos=(-141.288,-47.3075,-1.6) rot=(0.707107,0.707107,0;3.14159rad)
  LinkedObject = -> Shape004
  Placement = pos=(-141.288,-47.3075,-1.6) rot=(0.707107,0.707107,0;3.14159rad)
FEATURE [App::Link] D_2_D_SOD_123_611CB7E4_ln_018  label="D_83_2_D_SOD_123_611CBD45"
  LinkPlacement = pos=(144.463,-21.4635,-1.6) rot=(0.707107,0.707107,0;3.14159rad)
  LinkedObject = -> Shape004
  Placement = pos=(144.463,-21.4635,-1.6) rot=(0.707107,0.707107,0;3.14159rad)
FEATURE [App::Link] D_2_D_SOD_123_611CB7E4_ln_019  label="D_82_2_D_SOD_123_611CBD34"
  LinkPlacement = pos=(128.587,-28.2575,-1.6) rot=(0.707107,0.707107,0;3.14159rad)
  LinkedObject = -> Shape004
  Placement = pos=(128.587,-28.2575,-1.6) rot=(0.707107,0.707107,0;3.14159rad)
FEATURE [App::Link] D_2_D_SOD_123_611CB7E4_ln_020  label="D_81_2_D_SOD_123_611CBD23"
  LinkPlacement = pos=(125.413,-28.2575,-1.6) rot=(0.707107,0.707107,0;3.14159rad)
  LinkedObject = -> Shape004
  Placement = pos=(125.413,-28.2575,-1.6) rot=(0.707107,0.707107,0;3.14159rad)
FEATURE [App::Link] D_2_D_SOD_123_611CB7E4_ln_021  label="D_80_2_D_SOD_123_611CBD12"
  LinkPlacement = pos=(106.363,-28.1935,-1.6) rot=(0.707107,0.707107,0;3.14159rad)
  LinkedObject = -> Shape004
  Placement = pos=(106.363,-28.1935,-1.6) rot=(0.707107,0.707107,0;3.14159rad)
FEATURE [App::Link] D_2_D_SOD_123_611CB7E4_ln_022  label="D_79_2_D_SOD_123_611CBD01"
  LinkPlacement = pos=(87.313,-28.1935,-1.6) rot=(0.707107,0.707107,0;3.14159rad)
  LinkedObject = -> Shape004
  Placement = pos=(87.313,-28.1935,-1.6) rot=(0.707107,0.707107,0;3.14159rad)
FEATURE [App::Link] D_2_D_SOD_123_611CB7E4_ln_023  label="D_78_2_D_SOD_123_611CBCF0"
  LinkPlacement = pos=(68.263,-28.1935,-1.6) rot=(0.707107,0.707107,0;3.14159rad)
  LinkedObject = -> Shape004
  Placement = pos=(68.263,-28.1935,-1.6) rot=(0.707107,0.707107,0;3.14159rad)
FEATURE [App::Link] D_2_D_SOD_123_611CB7E4_ln_024  label="D_77_2_D_SOD_123_611CBCDF"
  LinkPlacement = pos=(49.213,-28.1935,-1.6) rot=(0.707107,0.707107,0;3.14159rad)
  LinkedObject = -> Shape004
  Placement = pos=(49.213,-28.1935,-1.6) rot=(0.707107,0.707107,0;3.14159rad)
FEATURE [App::Link] D_2_D_SOD_123_611CB7E4_ln_025  label="D_76_2_D_SOD_123_611CBCCE"
  LinkPlacement = pos=(30.163,-28.1935,-1.6) rot=(0.707107,0.707107,0;3.14159rad)
  LinkedObject = -> Shape004
  Placement = pos=(30.163,-28.1935,-1.6) rot=(0.707107,0.707107,0;3.14159rad)
FEATURE [App::Link] D_2_D_SOD_123_611CB7E4_ln_026  label="D_75_2_D_SOD_123_611CBCBD"
  LinkPlacement = pos=(11.113,-28.1935,-1.6) rot=(0.707107,0.707107,0;3.14159rad)
  LinkedObject = -> Shape004
  Placement = pos=(11.113,-28.1935,-1.6) rot=(0.707107,0.707107,0;3.14159rad)
FEATURE [App::Link] D_2_D_SOD_123_611CB7E4_ln_027  label="D_74_2_D_SOD_123_611CBCAC"
  LinkPlacement = pos=(-7.937,-28.1935,-1.6) rot=(0.707107,0.707107,0;3.14159rad)
  LinkedObject = -> Shape004
  Placement = pos=(-7.937,-28.1935,-1.6) rot=(0.707107,0.707107,0;3.14159rad)
FEATURE [App::Link] D_2_D_SOD_123_611CB7E4_ln_028  label="D_73_2_D_SOD_123_611CBC9B"
  LinkPlacement = pos=(-26.987,-28.1935,-1.6) rot=(0.707107,0.707107,0;3.14159rad)
  LinkedObject = -> Shape004
  Placement = pos=(-26.987,-28.1935,-1.6) rot=(0.707107,0.707107,0;3.14159rad)
FEATURE [App::Link] D_2_D_SOD_123_611CB7E4_ln_029  label="D_72_2_D_SOD_123_611CBC8A"
  LinkPlacement = pos=(-46.037,-28.1935,-1.6) rot=(0.707107,0.707107,0;3.14159rad)
  LinkedObject = -> Shape004
  Placement = pos=(-46.037,-28.1935,-1.6) rot=(0.707107,0.707107,0;3.14159rad)
FEATURE [App::Link] D_2_D_SOD_123_611CB7E4_ln_030  label="D_71_2_D_SOD_123_611CBC79"
  LinkPlacement = pos=(-65.087,-28.1935,-1.6) rot=(0.707107,0.707107,0;3.14159rad)
  LinkedObject = -> Shape004
  Placement = pos=(-65.087,-28.1935,-1.6) rot=(0.707107,0.707107,0;3.14159rad)
FEATURE [App::Link] D_2_D_SOD_123_611CB7E4_ln_031  label="D_70_2_D_SOD_123_611CBC68"
  LinkPlacement = pos=(-84.1375,-28.1935,-1.6) rot=(0.707107,0.707107,0;3.14159rad)
  LinkedObject = -> Shape004
  Placement = pos=(-84.1375,-28.1935,-1.6) rot=(0.707107,0.707107,0;3.14159rad)
FEATURE [App::Link] D_2_D_SOD_123_611CB7E4_ln_032  label="D_69_2_D_SOD_123_611CBC57"
  LinkPlacement = pos=(-103.124,-28.1935,-1.6) rot=(0.707107,0.707107,0;3.14159rad)
  LinkedObject = -> Shape004
  Placement = pos=(-103.124,-28.1935,-1.6) rot=(0.707107,0.707107,0;3.14159rad)
FEATURE [App::Link] D_2_D_SOD_123_611CB7E4_ln_033  label="D_68_2_D_SOD_123_611CBC46"
  LinkPlacement = pos=(-122.047,-28.0035,-1.6) rot=(0.707107,0.707107,0;3.14159rad)
  LinkedObject = -> Shape004
  Placement = pos=(-122.047,-28.0035,-1.6) rot=(0.707107,0.707107,0;3.14159rad)
FEATURE [App::Link] D_2_D_SOD_123_611CB7E4_ln_034  label="D_67_2_D_SOD_123_611CBC35"
  LinkPlacement = pos=(-141.224,-34.6075,-1.6) rot=(0.707107,0.707107,0;3.14159rad)
  LinkedObject = -> Shape004
  Placement = pos=(-141.224,-34.6075,-1.6) rot=(0.707107,0.707107,0;3.14159rad)
FEATURE [App::Link] D_2_D_SOD_123_611CB7E4_ln_035  label="D_66_2_D_SOD_123_611CBC24"
  LinkPlacement = pos=(144.589,-2.3495,-1.6) rot=(0.707107,0.707107,0;3.14159rad)
  LinkedObject = -> Shape004
  Placement = pos=(144.589,-2.3495,-1.6) rot=(0.707107,0.707107,0;3.14159rad)
FEATURE [App::Link] D_2_D_SOD_123_611CB7E4_ln_036  label="D_65_2_D_SOD_123_611CBC13"
  LinkPlacement = pos=(128.524,-9.144,-1.6) rot=(0.707107,0.707107,0;3.14159rad)
  LinkedObject = -> Shape004
  Placement = pos=(128.524,-9.144,-1.6) rot=(0.707107,0.707107,0;3.14159rad)
FEATURE [App::Link] D_2_D_SOD_123_611CB7E4_ln_037  label="D_64_2_D_SOD_123_611CBC02"
  LinkPlacement = pos=(125.476,-9.144,-1.6) rot=(0.707107,0.707107,0;3.14159rad)
  LinkedObject = -> Shape004
  Placement = pos=(125.476,-9.144,-1.6) rot=(0.707107,0.707107,0;3.14159rad)
FEATURE [App::Link] D_2_D_SOD_123_611CB7E4_ln_038  label="D_63_2_D_SOD_123_611CBBF1"
  LinkPlacement = pos=(106.426,-9.144,-1.6) rot=(0.707107,0.707107,0;3.14159rad)
  LinkedObject = -> Shape004
  Placement = pos=(106.426,-9.144,-1.6) rot=(0.707107,0.707107,0;3.14159rad)
FEATURE [App::Link] D_2_D_SOD_123_611CB7E4_ln_039  label="D_62_2_D_SOD_123_611CBBE0"
  LinkPlacement = pos=(87.376,-9.144,-1.6) rot=(0.707107,0.707107,0;3.14159rad)
  LinkedObject = -> Shape004
  Placement = pos=(87.376,-9.144,-1.6) rot=(0.707107,0.707107,0;3.14159rad)
FEATURE [App::Link] D_2_D_SOD_123_611CB7E4_ln_040  label="D_61_2_D_SOD_123_611CBBCF"
  LinkPlacement = pos=(68.263,-9.144,-1.6) rot=(0.707107,0.707107,0;3.14159rad)
  LinkedObject = -> Shape004
  Placement = pos=(68.263,-9.144,-1.6) rot=(0.707107,0.707107,0;3.14159rad)
FEATURE [App::Link] D_2_D_SOD_123_611CB7E4_ln_041  label="D_60_2_D_SOD_123_611CBBBE"
  LinkPlacement = pos=(49.276,-9.144,-1.6) rot=(0.707107,0.707107,0;3.14159rad)
  LinkedObject = -> Shape004
  Placement = pos=(49.276,-9.144,-1.6) rot=(0.707107,0.707107,0;3.14159rad)
FEATURE [App::Link] D_2_D_SOD_123_611CB7E4_ln_042  label="D_59_2_D_SOD_123_611CBBAD"
  LinkPlacement = pos=(30.226,-9.144,-1.6) rot=(0.707107,0.707107,0;3.14159rad)
  LinkedObject = -> Shape004
  Placement = pos=(30.226,-9.144,-1.6) rot=(0.707107,0.707107,0;3.14159rad)
FEATURE [App::Link] D_2_D_SOD_123_611CB7E4_ln_043  label="D_58_2_D_SOD_123_611CBB9C"
  LinkPlacement = pos=(11.176,-9.2075,-1.6) rot=(0.707107,0.707107,0;3.14159rad)
  LinkedObject = -> Shape004
  Placement = pos=(11.176,-9.2075,-1.6) rot=(0.707107,0.707107,0;3.14159rad)
FEATURE [App::Link] D_2_D_SOD_123_611CB7E4_ln_044  label="D_57_2_D_SOD_123_611CBB8B"
  LinkPlacement = pos=(-7.874,-9.144,-1.6) rot=(0.707107,0.707107,0;3.14159rad)
  LinkedObject = -> Shape004
  Placement = pos=(-7.874,-9.144,-1.6) rot=(0.707107,0.707107,0;3.14159rad)
FEATURE [App::Link] D_2_D_SOD_123_611CB7E4_ln_045  label="D_56_2_D_SOD_123_611CBB7A"
  LinkPlacement = pos=(-26.924,-9.144,-1.6) rot=(0.707107,0.707107,0;3.14159rad)
  LinkedObject = -> Shape004
  Placement = pos=(-26.924,-9.144,-1.6) rot=(0.707107,0.707107,0;3.14159rad)
FEATURE [App::Link] D_2_D_SOD_123_611CB7E4_ln_046  label="D_55_2_D_SOD_123_611CBB69"
  LinkPlacement = pos=(-45.974,-9.144,-1.6) rot=(0.707107,0.707107,0;3.14159rad)
  LinkedObject = -> Shape004
  Placement = pos=(-45.974,-9.144,-1.6) rot=(0.707107,0.707107,0;3.14159rad)
FEATURE [App::Link] D_2_D_SOD_123_611CB7E4_ln_047  label="D_54_2_D_SOD_123_611CBB58"
  LinkPlacement = pos=(-80.899,-9.144,-1.6) rot=(0.707107,0.707107,0;3.14159rad)
  LinkedObject = -> Shape004
  Placement = pos=(-80.899,-9.144,-1.6) rot=(0.707107,0.707107,0;3.14159rad)
FEATURE [App::Link] D_2_D_SOD_123_611CB7E4_ln_048  label="D_53_2_D_SOD_123_611CBB47"
  LinkPlacement = pos=(-84.074,-9.144,-1.6) rot=(0.707107,0.707107,0;3.14159rad)
  LinkedObject = -> Shape004
  Placement = pos=(-84.074,-9.144,-1.6) rot=(0.707107,0.707107,0;3.14159rad)
FEATURE [App::Link] D_2_D_SOD_123_611CB7E4_ln_049  label="D_52_2_D_SOD_123_611CBB36"
  LinkPlacement = pos=(-103.124,-8.509,-1.6) rot=(0.707107,0.707107,0;3.14159rad)
  LinkedObject = -> Shape004
  Placement = pos=(-103.124,-8.509,-1.6) rot=(0.707107,0.707107,0;3.14159rad)
FEATURE [App::Link] D_2_D_SOD_123_611CB7E4_ln_050  label="D_51_2_D_SOD_123_611CBB25"
  LinkPlacement = pos=(-122.047,-9.2075,-1.6) rot=(0.707107,0.707107,0;3.14159rad)
  LinkedObject = -> Shape004
  Placement = pos=(-122.047,-9.2075,-1.6) rot=(0.707107,0.707107,0;3.14159rad)
FEATURE [App::Link] D_2_D_SOD_123_611CB7E4_ln_051  label="D_50_2_D_SOD_123_611CBB14"
  LinkPlacement = pos=(-141.224,-15.4305,-1.6) rot=(0.707107,0.707107,0;3.14159rad)
  LinkedObject = -> Shape004
  Placement = pos=(-141.224,-15.4305,-1.6) rot=(0.707107,0.707107,0;3.14159rad)
FEATURE [App::Link] D_2_D_SOD_123_611CB7E4_ln_052  label="D_49_2_D_SOD_123_611CBB03"
  LinkPlacement = pos=(147.574,9.906,-1.6) rot=(0.707107,0.707107,0;3.14159rad)
  LinkedObject = -> Shape004
  Placement = pos=(147.574,9.906,-1.6) rot=(0.707107,0.707107,0;3.14159rad)
FEATURE [App::Link] D_2_D_SOD_123_611CB7E4_ln_053  label="D_48_2_D_SOD_123_611CBAF2"
  LinkPlacement = pos=(144.526,9.906,-1.6) rot=(0.707107,0.707107,0;3.14159rad)
  LinkedObject = -> Shape004
  Placement = pos=(144.526,9.906,-1.6) rot=(0.707107,0.707107,0;3.14159rad)
FEATURE [App::Link] D_2_D_SOD_123_611CB7E4_ln_054  label="D_47_2_D_SOD_123_611CBAE1"
  LinkPlacement = pos=(125.476,9.906,-1.6) rot=(0.707107,0.707107,0;3.14159rad)
  LinkedObject = -> Shape004
  Placement = pos=(125.476,9.906,-1.6) rot=(0.707107,0.707107,0;3.14159rad)
FEATURE [App::Link] D_2_D_SOD_123_611CB7E4_ln_055  label="D_46_2_D_SOD_123_611CBAD0"
  LinkPlacement = pos=(106.426,9.906,-1.6) rot=(0.707107,0.707107,0;3.14159rad)
  LinkedObject = -> Shape004
  Placement = pos=(106.426,9.906,-1.6) rot=(0.707107,0.707107,0;3.14159rad)
FEATURE [App::Link] D_2_D_SOD_123_611CB7E4_ln_056  label="D_45_2_D_SOD_123_611CBABF"
  LinkPlacement = pos=(87.376,9.906,-1.6) rot=(0.707107,0.707107,0;3.14159rad)
  LinkedObject = -> Shape004
  Placement = pos=(87.376,9.906,-1.6) rot=(0.707107,0.707107,0;3.14159rad)
FEATURE [App::Link] D_2_D_SOD_123_611CB7E4_ln_057  label="D_44_2_D_SOD_123_611CBAAE"
  LinkPlacement = pos=(68.326,9.906,-1.6) rot=(0.707107,0.707107,0;3.14159rad)
  LinkedObject = -> Shape004
  Placement = pos=(68.326,9.906,-1.6) rot=(0.707107,0.707107,0;3.14159rad)
FEATURE [App::Link] D_2_D_SOD_123_611CB7E4_ln_058  label="D_43_2_D_SOD_123_611CBA9D"
  LinkPlacement = pos=(49.276,9.906,-1.6) rot=(0.707107,0.707107,0;3.14159rad)
  LinkedObject = -> Shape004
  Placement = pos=(49.276,9.906,-1.6) rot=(0.707107,0.707107,0;3.14159rad)
FEATURE [App::Link] D_2_D_SOD_123_611CB7E4_ln_059  label="D_42_2_D_SOD_123_611CBA8C"
  LinkPlacement = pos=(30.226,9.906,-1.6) rot=(0.707107,0.707107,0;3.14159rad)
  LinkedObject = -> Shape004
  Placement = pos=(30.226,9.906,-1.6) rot=(0.707107,0.707107,0;3.14159rad)
FEATURE [App::Link] D_2_D_SOD_123_611CB7E4_ln_060  label="D_41_2_D_SOD_123_611CBA7B"
  LinkPlacement = pos=(11.176,9.906,-1.6) rot=(0.707107,0.707107,0;3.14159rad)
  LinkedObject = -> Shape004
  Placement = pos=(11.176,9.906,-1.6) rot=(0.707107,0.707107,0;3.14159rad)
FEATURE [App::Link] D_2_D_SOD_123_611CB7E4_ln_061  label="D_40_2_D_SOD_123_611CBA6A"
  LinkPlacement = pos=(-7.874,9.906,-1.6) rot=(0.707107,0.707107,0;3.14159rad)
  LinkedObject = -> Shape004
  Placement = pos=(-7.874,9.906,-1.6) rot=(0.707107,0.707107,0;3.14159rad)
FEATURE [App::Link] D_2_D_SOD_123_611CB7E4_ln_062  label="D_39_2_D_SOD_123_611CBA59"
  LinkPlacement = pos=(-26.924,9.906,-1.6) rot=(0.707107,0.707107,0;3.14159rad)
  LinkedObject = -> Shape004
  Placement = pos=(-26.924,9.906,-1.6) rot=(0.707107,0.707107,0;3.14159rad)
FEATURE [App::Link] D_2_D_SOD_123_611CB7E4_ln_063  label="D_38_2_D_SOD_123_611CBA48"
  LinkPlacement = pos=(-45.974,9.906,-1.6) rot=(0.707107,0.707107,0;3.14159rad)
  LinkedObject = -> Shape004
  Placement = pos=(-45.974,9.906,-1.6) rot=(0.707107,0.707107,0;3.14159rad)
FEATURE [App::Link] D_2_D_SOD_123_611CB7E4_ln_064  label="D_37_2_D_SOD_123_611CBA37"
  LinkPlacement = pos=(-80.899,9.906,-1.6) rot=(0.707107,0.707107,0;3.14159rad)
  LinkedObject = -> Shape004
  Placement = pos=(-80.899,9.906,-1.6) rot=(0.707107,0.707107,0;3.14159rad)
FEATURE [App::Link] D_2_D_SOD_123_611CB7E4_ln_065  label="D_36_2_D_SOD_123_611CBA26"
  LinkPlacement = pos=(-84.074,9.906,-1.6) rot=(0.707107,0.707107,0;3.14159rad)
  LinkedObject = -> Shape004
  Placement = pos=(-84.074,9.906,-1.6) rot=(0.707107,0.707107,0;3.14159rad)
FEATURE [App::Link] D_2_D_SOD_123_611CB7E4_ln_066  label="D_35_2_D_SOD_123_611CBA15"
  LinkPlacement = pos=(-103.124,9.906,-1.6) rot=(0.707107,0.707107,0;3.14159rad)
  LinkedObject = -> Shape004
  Placement = pos=(-103.124,9.906,-1.6) rot=(0.707107,0.707107,0;3.14159rad)
FEATURE [App::Link] D_2_D_SOD_123_611CB7E4_ln_067  label="D_34_2_D_SOD_123_611CBA04"
  LinkPlacement = pos=(-122.047,9.9695,-1.6) rot=(0.707107,0.707107,0;3.14159rad)
  LinkedObject = -> Shape004
  Placement = pos=(-122.047,9.9695,-1.6) rot=(0.707107,0.707107,0;3.14159rad)
FEATURE [App::Link] D_2_D_SOD_123_611CB7E4_ln_068  label="D_33_2_D_SOD_123_611CB9F3"
  LinkPlacement = pos=(-141.097,3.4925,-1.6) rot=(0.707107,0.707107,0;3.14159rad)
  LinkedObject = -> Shape004
  Placement = pos=(-141.097,3.4925,-1.6) rot=(0.707107,0.707107,0;3.14159rad)
FEATURE [App::Link] D_2_D_SOD_123_611CB7E4_ln_069  label="D_32_2_D_SOD_123_611CB9E2"
  LinkPlacement = pos=(147.511,28.0035,-1.6) rot=(0.707107,0.707107,0;3.14159rad)
  LinkedObject = -> Shape004
  Placement = pos=(147.511,28.0035,-1.6) rot=(0.707107,0.707107,0;3.14159rad)
FEATURE [App::Link] D_2_D_SOD_123_611CB7E4_ln_070  label="D_31_2_D_SOD_123_611CB9D1"
  LinkPlacement = pos=(125.921,36.2585,-1.6) rot=(0.707107,0.707107,0;3.14159rad)
  LinkedObject = -> Shape004
  Placement = pos=(125.921,36.2585,-1.6) rot=(0.707107,0.707107,0;3.14159rad)
FEATURE [App::Link] D_2_D_SOD_123_611CB7E4_ln_071  label="D_30_2_D_SOD_123_611CB9C0"
  LinkPlacement = pos=(109.474,28.321,-1.6) rot=(0.707107,0.707107,0;3.14159rad)
  LinkedObject = -> Shape004
  Placement = pos=(109.474,28.321,-1.6) rot=(0.707107,0.707107,0;3.14159rad)
FEATURE [App::Link] D_2_D_SOD_123_611CB7E4_ln_072  label="D_29_2_D_SOD_123_611CB9AF"
  LinkPlacement = pos=(106.426,28.321,-1.6) rot=(0.707107,0.707107,0;3.14159rad)
  LinkedObject = -> Shape004
  Placement = pos=(106.426,28.321,-1.6) rot=(0.707107,0.707107,0;3.14159rad)
FEATURE [App::Link] D_2_D_SOD_123_611CB7E4_ln_073  label="D_28_2_D_SOD_123_611CB99E"
  LinkPlacement = pos=(87.376,28.321,-1.6) rot=(0.707107,0.707107,0;3.14159rad)
  LinkedObject = -> Shape004
  Placement = pos=(87.376,28.321,-1.6) rot=(0.707107,0.707107,0;3.14159rad)
FEATURE [App::Link] D_2_D_SOD_123_611CB7E4_ln_074  label="D_27_2_D_SOD_123_611CB98D"
  LinkPlacement = pos=(68.326,28.2575,-1.6) rot=(0.707107,0.707107,0;3.14159rad)
  LinkedObject = -> Shape004
  Placement = pos=(68.326,28.2575,-1.6) rot=(0.707107,0.707107,0;3.14159rad)
FEATURE [App::Link] D_2_D_SOD_123_611CB7E4_ln_075  label="D_26_2_D_SOD_123_611CB97C"
  LinkPlacement = pos=(49.276,28.321,-1.6) rot=(0.707107,0.707107,0;3.14159rad)
  LinkedObject = -> Shape004
  Placement = pos=(49.276,28.321,-1.6) rot=(0.707107,0.707107,0;3.14159rad)
FEATURE [App::Link] D_2_D_SOD_123_611CB7E4_ln_076  label="D_25_2_D_SOD_123_611CB96B"
  LinkPlacement = pos=(30.226,28.2575,-1.6) rot=(0.707107,0.707107,0;3.14159rad)
  LinkedObject = -> Shape004
  Placement = pos=(30.226,28.2575,-1.6) rot=(0.707107,0.707107,0;3.14159rad)
FEATURE [App::Link] D_2_D_SOD_123_611CB7E4_ln_077  label="D_24_2_D_SOD_123_611CB95A"
  LinkPlacement = pos=(11.176,28.2575,-1.6) rot=(0.707107,0.707107,0;3.14159rad)
  LinkedObject = -> Shape004
  Placement = pos=(11.176,28.2575,-1.6) rot=(0.707107,0.707107,0;3.14159rad)
FEATURE [App::Link] D_2_D_SOD_123_611CB7E4_ln_078  label="D_23_2_D_SOD_123_611CB949"
  LinkPlacement = pos=(-7.874,28.321,-1.6) rot=(0.707107,0.707107,0;3.14159rad)
  LinkedObject = -> Shape004
  Placement = pos=(-7.874,28.321,-1.6) rot=(0.707107,0.707107,0;3.14159rad)
FEATURE [App::Link] D_2_D_SOD_123_611CB7E4_ln_079  label="D_22_2_D_SOD_123_611CB938"
  LinkPlacement = pos=(-26.924,28.321,-1.6) rot=(0.707107,0.707107,0;3.14159rad)
  LinkedObject = -> Shape004
  Placement = pos=(-26.924,28.321,-1.6) rot=(0.707107,0.707107,0;3.14159rad)
FEATURE [App::Link] D_2_D_SOD_123_611CB7E4_ln_080  label="D_21_2_D_SOD_123_611CB927"
  LinkPlacement = pos=(-45.974,28.321,-1.6) rot=(0.707107,0.707107,0;3.14159rad)
  LinkedObject = -> Shape004
  Placement = pos=(-45.974,28.321,-1.6) rot=(0.707107,0.707107,0;3.14159rad)
FEATURE [App::Link] D_2_D_SOD_123_611CB7E4_ln_081  label="D_20_2_D_SOD_123_611CB916"
  LinkPlacement = pos=(-65.024,28.2575,-1.6) rot=(0.707107,0.707107,0;3.14159rad)
  LinkedObject = -> Shape004
  Placement = pos=(-65.024,28.2575,-1.6) rot=(0.707107,0.707107,0;3.14159rad)
FEATURE [App::Link] D_2_D_SOD_123_611CB7E4_ln_082  label="D_19_2_D_SOD_123_611CB905"
  LinkPlacement = pos=(-84.074,28.321,-1.6) rot=(0.707107,0.707107,0;3.14159rad)
  LinkedObject = -> Shape004
  Placement = pos=(-84.074,28.321,-1.6) rot=(0.707107,0.707107,0;3.14159rad)
FEATURE [App::Link] D_2_D_SOD_123_611CB7E4_ln_083  label="D_18_2_D_SOD_123_611CB8F4"
  LinkPlacement = pos=(-103.124,28.2575,-1.6) rot=(0.707107,0.707107,0;3.14159rad)
  LinkedObject = -> Shape004
  Placement = pos=(-103.124,28.2575,-1.6) rot=(0.707107,0.707107,0;3.14159rad)
FEATURE [App::Link] D_2_D_SOD_123_611CB7E4_ln_084  label="D_17_2_D_SOD_123_611CB8E3"
  LinkPlacement = pos=(-122.174,28.2575,-1.6) rot=(0.707107,0.707107,0;3.14159rad)
  LinkedObject = -> Shape004
  Placement = pos=(-122.174,28.2575,-1.6) rot=(0.707107,0.707107,0;3.14159rad)
FEATURE [App::Link] D_2_D_SOD_123_611CB7E4_ln_085  label="D_16_2_D_SOD_123_611CB8D2"
  LinkPlacement = pos=(128.524,47.371,-1.6) rot=(0.707107,0.707107,0;3.14159rad)
  LinkedObject = -> Shape004
  Placement = pos=(128.524,47.371,-1.6) rot=(0.707107,0.707107,0;3.14159rad)
FEATURE [App::Link] D_2_D_SOD_123_611CB7E4_ln_086  label="D_15_2_D_SOD_123_611CB8C1"
  LinkPlacement = pos=(125.476,47.371,-1.6) rot=(0.707107,0.707107,0;3.14159rad)
  LinkedObject = -> Shape004
  Placement = pos=(125.476,47.371,-1.6) rot=(0.707107,0.707107,0;3.14159rad)
FEATURE [App::Link] D_2_D_SOD_123_611CB7E4_ln_087  label="D_14_2_D_SOD_123_611CB8B0"
  LinkPlacement = pos=(106.426,47.371,-1.6) rot=(0.707107,0.707107,0;3.14159rad)
  LinkedObject = -> Shape004
  Placement = pos=(106.426,47.371,-1.6) rot=(0.707107,0.707107,0;3.14159rad)
FEATURE [App::Link] D_2_D_SOD_123_611CB7E4_ln_088  label="D_13_2_D_SOD_123_611CB89F"
  LinkPlacement = pos=(87.376,47.371,-1.6) rot=(0.707107,0.707107,0;3.14159rad)
  LinkedObject = -> Shape004
  Placement = pos=(87.376,47.371,-1.6) rot=(0.707107,0.707107,0;3.14159rad)
FEATURE [App::Link] D_2_D_SOD_123_611CB7E4_ln_089  label="D_12_2_D_SOD_123_611CB88E"
  LinkPlacement = pos=(68.326,47.371,-1.6) rot=(0.707107,0.707107,0;3.14159rad)
  LinkedObject = -> Shape004
  Placement = pos=(68.326,47.371,-1.6) rot=(0.707107,0.707107,0;3.14159rad)
FEATURE [App::Link] D_2_D_SOD_123_611CB7E4_ln_090  label="D_11_2_D_SOD_123_611CB87D"
  LinkPlacement = pos=(49.276,47.371,-1.6) rot=(0.707107,0.707107,0;3.14159rad)
  LinkedObject = -> Shape004
  Placement = pos=(49.276,47.371,-1.6) rot=(0.707107,0.707107,0;3.14159rad)
FEATURE [App::Link] D_2_D_SOD_123_611CB7E4_ln_091  label="D_10_2_D_SOD_123_611CB86C"
  LinkPlacement = pos=(30.226,47.371,-1.6) rot=(0.707107,0.707107,0;3.14159rad)
  LinkedObject = -> Shape004
  Placement = pos=(30.226,47.371,-1.6) rot=(0.707107,0.707107,0;3.14159rad)
FEATURE [App::Link] D_2_D_SOD_123_611CB7E4_ln_092  label="D_9_2_D_SOD_123_611CB85B"
  LinkPlacement = pos=(11.176,47.371,-1.6) rot=(0.707107,0.707107,0;3.14159rad)
  LinkedObject = -> Shape004
  Placement = pos=(11.176,47.371,-1.6) rot=(0.707107,0.707107,0;3.14159rad)
FEATURE [App::Link] D_2_D_SOD_123_611CB7E4_ln_093  label="D_8_2_D_SOD_123_611CB84A"
  LinkPlacement = pos=(-7.874,47.371,-1.6) rot=(0.707107,0.707107,0;3.14159rad)
  LinkedObject = -> Shape004
  Placement = pos=(-7.874,47.371,-1.6) rot=(0.707107,0.707107,0;3.14159rad)
FEATURE [App::Link] D_2_D_SOD_123_611CB7E4_ln_094  label="D_7_2_D_SOD_123_611CB839"
  LinkPlacement = pos=(-26.924,47.371,-1.6) rot=(0.707107,0.707107,0;3.14159rad)
  LinkedObject = -> Shape004
  Placement = pos=(-26.924,47.371,-1.6) rot=(0.707107,0.707107,0;3.14159rad)
FEATURE [App::Link] D_2_D_SOD_123_611CB7E4_ln_095  label="D_6_2_D_SOD_123_611CB828"
  LinkPlacement = pos=(-45.974,47.371,-1.6) rot=(0.707107,0.707107,0;3.14159rad)
  LinkedObject = -> Shape004
  Placement = pos=(-45.974,47.371,-1.6) rot=(0.707107,0.707107,0;3.14159rad)
FEATURE [App::Link] D_2_D_SOD_123_611CB7E4_ln_096  label="D_5_2_D_SOD_123_611CB817"
  LinkPlacement = pos=(-65.024,46.736,-1.6) rot=(0.707107,0.707107,0;3.14159rad)
  LinkedObject = -> Shape004
  Placement = pos=(-65.024,46.736,-1.6) rot=(0.707107,0.707107,0;3.14159rad)
FEATURE [App::Link] D_2_D_SOD_123_611CB7E4_ln_097  label="D_4_2_D_SOD_123_611CB806"
  LinkPlacement = pos=(-84.1375,47.371,-1.6) rot=(0.707107,0.707107,0;3.14159rad)
  LinkedObject = -> Shape004
  Placement = pos=(-84.1375,47.371,-1.6) rot=(0.707107,0.707107,0;3.14159rad)
FEATURE [App::Link] D_2_D_SOD_123_611CB7E4_ln_098  label="D_3_2_D_SOD_123_611CB7F5"
  LinkPlacement = pos=(-103.188,47.371,-1.6) rot=(0.707107,0.707107,0;3.14159rad)
  LinkedObject = -> Shape004
  Placement = pos=(-103.188,47.371,-1.6) rot=(0.707107,0.707107,0;3.14159rad)
FEATURE [App::Link] D_2_D_SOD_123_611CB7E4_ln_099  label="D26_2_D_SOD_123_611CB7C2"
  LinkPlacement = pos=(-142.24,22.2885,-1.6) rot=(0.707107,0.707107,0;3.14159rad)
  LinkedObject = -> Shape004
  Placement = pos=(-142.24,22.2885,-1.6) rot=(0.707107,0.707107,0;3.14159rad)
FEATURE [Part::Feature] Shape005  label="D3_LED_WS2812B_PLCC4_50x50mm_P32mm_611CB5AF"
  Placement = pos=(3.175,19.05,-1.6) rot=(0,1,0;3.14159rad)
  shape: bbox 5.4 x 5 x 1.6 mm, 68 faces (baked)
FEATURE [Part::Feature] Part__Feature007  label="SOLID001"
  shape: bbox 13.86 x 30.2 x 14.85 mm, 421 faces (baked)
FEATURE [Part::Feature] Part__Feature008  label="COMPOUND"
  shape: bbox 8.6 x 30.2 x 10 mm, 0 faces, 0 solids (baked)
FEATURE [App::Part] PEC11R_4220K_L13_8_W12_4_H26_5  label="K_1_PEC11R-4220K_L13-8_W12-4_H26-5_611CBEC7"
  Group = -> [Part__Feature007,Part__Feature008]
  Origin = -> Origin010
  Placement = pos=(136.525,47.625,0) rot=(1,0,0;1.5708rad)
FEATURE [Part::Feature] Shape006  label="K_1_Rotary knob v4_611CBEC7[2]"
  Placement = pos=(136.525,47.625,10) rot=(1,0,0;1.5708rad)
  shape: bbox 12 x 12 x 18 mm, 33 faces (baked)
FEATURE [App::Part] Top_e1db
  Group = -> [Shape,Shape001,K_105_cherry_mx_611CBFA4_ln_,K_105_MX______________________________________1_______611CBFA4_2__ln_,K_105_cherry_mx_611CBFA4_ln_001,K_105_MX______________________________________1_______611CBFA4_2__ln_001,K_105_cherry_mx_611CBFA4_ln_002,K_105_MX______________________________________1_______611CBFA4_2__ln_002,K_105_cherry_mx_611CBFA4_ln_003,+205 more]
  Origin = -> Origin003
FEATURE [Part::Feature] Shape007  label="J1_(Unsaved)_611F973D"
  Placement = pos=(-165.556,28.575,-1.6) rot=(0.707107,0.707107,0;3.14159rad)
  shape: bbox 7.903 x 8.943 x 4.203 mm, 384 faces, 24 solids (baked)
FEATURE [Part::Feature] Shape008  label="Y1_Crystal_SMD_3225-4Pin_3.2x2.5mm_611CC0DE"
  Placement = pos=(-53.403,0.9525,-1.6) rot=(0.92388,0.382683,0;3.14159rad)
  shape: bbox 3.891 x 3.889 x 0.64 mm, 28 faces (baked)
FEATURE [Part::Feature] Shape009  label="U3_LQFP_64_10x10mm_P05mm_611CC0CC"
  Placement = pos=(-64.135,1.7145,-1.6) rot=(0,1,0;3.14159rad)
  shape: bbox 12 x 12 x 1.5 mm, 1004 faces (baked)
FEATURE [Part::Feature] Shape010  label="U2_SOT_23_6_611CC061"
  Placement = pos=(-157.162,28.575,-1.6) rot=(1,0,0;3.14159rad)
  shape: bbox 2.8 x 2.9 x 1.55 mm, 124 faces (baked)
FEATURE [Part::Feature] Shape011  label="U1_SOT_23_5_611CC04B"
  Placement = pos=(-82.55,19.05,-1.6) rot=(1,0,0;3.14159rad)
  shape: bbox 2.8 x 2.9 x 1.55 mm, 109 faces (baked)
FEATURE [Part::Feature] Shape012  label="SW1_EVQPUC02K_611CC036"
  Placement = pos=(-158.75,42.8625,-1.6) rot=(0.57735,0.57735,-0.57735;4.18879rad)
  shape: bbox 4.542 x 6.402 x 2.183 mm, 274 faces (baked)
FEATURE [App::Link] R7_R_0603_1608Metric_611CC01B_ln_011  label="R5_R_0603_1608Metric_611CC007"
  LinkPlacement = pos=(-73.279,3.3655,-1.6) rot=(0,1,0;3.14159rad)
  LinkedObject = -> Shape002
  Placement = pos=(-73.279,3.3655,-1.6) rot=(0,1,0;3.14159rad)
FEATURE [Part::Feature] Shape013  label="Q2_SOT_23_611CBFCE"
  Placement = pos=(-143.256,27.305,-1.6) rot=(0.707107,0.707107,0;3.14159rad)
  shape: bbox 3 x 2.5 x 1.2 mm, 76 faces (baked)
FEATURE [App::Link] Q2_SOT_23_611CBFCE_ln_  label="Q1_SOT_23_611CBFB9"
  LinkPlacement = pos=(-98.425,38.1,-1.6) rot=(0,1,0;3.14159rad)
  LinkedObject = -> Shape013
  Placement = pos=(-98.425,38.1,-1.6) rot=(0,1,0;3.14159rad)
FEATURE [Part::Feature] Shape014  label="J2_PinHeader_1x06_P254mm_Vertical_611CBEB1"
  Placement = pos=(-147.828,33.9725,-1.6) rot=(0,1,0;3.14159rad)
  shape: bbox 2.54 x 15.24 x 11.54 mm, 148 faces (baked)
FEATURE [Part::Feature] Shape015  label="F1_User Library-ptc06032-1_611CBE77"
  Placement = pos=(-151.939,32.8295,-1.6) rot=(0,1,0;3.14159rad)
  shape: bbox 1.6 x 0.75 x 0.755 mm, 42 faces (baked)
FEATURE [App::Link] D3_LED_WS2812B_PLCC4_50x50mm_P32mm_611CB5AF_ln_  label="D20_LED_WS2812B_PLCC4_50x50mm_P32mm_611CB736"
  LinkPlacement = pos=(-101.6,-38.0995,-1.6) rot=(0,1,0;3.14159rad)
  LinkedObject = -> Shape005
  Placement = pos=(-101.6,-38.0995,-1.6) rot=(0,1,0;3.14159rad)
FEATURE [App::Link] D3_LED_WS2812B_PLCC4_50x50mm_P32mm_611CB5AF_ln_001  label="D19_LED_WS2812B_PLCC4_50x50mm_P32mm_611CB71F"
  LinkPlacement = pos=(-44.577,-38.0995,-1.6) rot=(0,1,0;3.14159rad)
  LinkedObject = -> Shape005
  Placement = pos=(-44.577,-38.0995,-1.6) rot=(0,1,0;3.14159rad)
FEATURE [App::Link] D3_LED_WS2812B_PLCC4_50x50mm_P32mm_611CB5AF_ln_002  label="D18_LED_WS2812B_PLCC4_50x50mm_P32mm_611CB708"
  LinkPlacement = pos=(3.175,-38.0995,-1.6) rot=(0,1,0;3.14159rad)
  LinkedObject = -> Shape005
  Placement = pos=(3.175,-38.0995,-1.6) rot=(0,1,0;3.14159rad)
FEATURE [App::Link] D3_LED_WS2812B_PLCC4_50x50mm_P32mm_611CB5AF_ln_003  label="D17_LED_WS2812B_PLCC4_50x50mm_P32mm_611CB6F1"
  LinkPlacement = pos=(69.799,-38.1245,-1.6) rot=(0,1,0;3.14159rad)
  LinkedObject = -> Shape005
  Placement = pos=(69.799,-38.1245,-1.6) rot=(0,1,0;3.14159rad)
FEATURE [App::Link] D3_LED_WS2812B_PLCC4_50x50mm_P32mm_611CB5AF_ln_004  label="D16_LED_WS2812B_PLCC4_50x50mm_P32mm_611CB6DA"
  LinkPlacement = pos=(127,-38.0995,-1.6) rot=(0,1,0;3.14159rad)
  LinkedObject = -> Shape005
  Placement = pos=(127,-38.0995,-1.6) rot=(0,1,0;3.14159rad)
FEATURE [App::Link] D3_LED_WS2812B_PLCC4_50x50mm_P32mm_611CB5AF_ln_005  label="D15_LED_WS2812B_PLCC4_50x50mm_P32mm_611CB6C3"
  LinkPlacement = pos=(127,-19.0495,-1.6) rot=(0,1,0;3.14159rad)
  LinkedObject = -> Shape005
  Placement = pos=(127,-19.0495,-1.6) rot=(0,1,0;3.14159rad)
FEATURE [App::Link] D3_LED_WS2812B_PLCC4_50x50mm_P32mm_611CB5AF_ln_006  label="D14_LED_WS2812B_PLCC4_50x50mm_P32mm_611CB6AC"
  LinkPlacement = pos=(69.85,-19.0495,-1.6) rot=(0,1,0;3.14159rad)
  LinkedObject = -> Shape005
  Placement = pos=(69.85,-19.0495,-1.6) rot=(0,1,0;3.14159rad)
FEATURE [App::Link] D3_LED_WS2812B_PLCC4_50x50mm_P32mm_611CB5AF_ln_007  label="D13_LED_WS2812B_PLCC4_50x50mm_P32mm_611CB695"
  LinkPlacement = pos=(3.175,-19.0495,-1.6) rot=(0,1,0;3.14159rad)
  LinkedObject = -> Shape005
  Placement = pos=(3.175,-19.0495,-1.6) rot=(0,1,0;3.14159rad)
FEATURE [App::Link] D3_LED_WS2812B_PLCC4_50x50mm_P32mm_611CB5AF_ln_008  label="D12_LED_WS2812B_PLCC4_50x50mm_P32mm_611CB67E"
  LinkPlacement = pos=(-44.45,-19.0495,-1.6) rot=(0,1,0;3.14159rad)
  LinkedObject = -> Shape005
  Placement = pos=(-44.45,-19.0495,-1.6) rot=(0,1,0;3.14159rad)
FEATURE [App::Link] D3_LED_WS2812B_PLCC4_50x50mm_P32mm_611CB5AF_ln_009  label="D11_LED_WS2812B_PLCC4_50x50mm_P32mm_611CB667"
  LinkPlacement = pos=(-101.6,-19.0495,-1.6) rot=(0,1,0;3.14159rad)
  LinkedObject = -> Shape005
  Placement = pos=(-101.6,-19.0495,-1.6) rot=(0,1,0;3.14159rad)
FEATURE [App::Link] D3_LED_WS2812B_PLCC4_50x50mm_P32mm_611CB5AF_ln_010  label="D10_LED_WS2812B_PLCC4_50x50mm_P32mm_611CB650"
  LinkPlacement = pos=(-101.6,0,-1.6) rot=(0,1,0;3.14159rad)
  LinkedObject = -> Shape005
  Placement = pos=(-101.6,0,-1.6) rot=(0,1,0;3.14159rad)
FEATURE [App::Link] D3_LED_WS2812B_PLCC4_50x50mm_P32mm_611CB5AF_ln_011  label="D9_LED_WS2812B_PLCC4_50x50mm_P32mm_611CB639"
  LinkPlacement = pos=(-44.45,0,-1.6) rot=(0,1,0;3.14159rad)
  LinkedObject = -> Shape005
  Placement = pos=(-44.45,0,-1.6) rot=(0,1,0;3.14159rad)
FEATURE [App::Link] D3_LED_WS2812B_PLCC4_50x50mm_P32mm_611CB5AF_ln_012  label="D8_LED_WS2812B_PLCC4_50x50mm_P32mm_611CB622"
  LinkPlacement = pos=(3.175,0,-1.6) rot=(0,1,0;3.14159rad)
  LinkedObject = -> Shape005
  Placement = pos=(3.175,0,-1.6) rot=(0,1,0;3.14159rad)
FEATURE [App::Link] D3_LED_WS2812B_PLCC4_50x50mm_P32mm_611CB5AF_ln_013  label="D7_LED_WS2812B_PLCC4_50x50mm_P32mm_611CB60B"
  LinkPlacement = pos=(69.85,0,-1.6) rot=(0,1,0;3.14159rad)
  LinkedObject = -> Shape005
  Placement = pos=(69.85,0,-1.6) rot=(0,1,0;3.14159rad)
FEATURE [App::Link] D3_LED_WS2812B_PLCC4_50x50mm_P32mm_611CB5AF_ln_014  label="D6_LED_WS2812B_PLCC4_50x50mm_P32mm_611CB5F4"
  LinkPlacement = pos=(127,0,-1.6) rot=(0,1,0;3.14159rad)
  LinkedObject = -> Shape005
  Placement = pos=(127,0,-1.6) rot=(0,1,0;3.14159rad)
FEATURE [App::Link] D3_LED_WS2812B_PLCC4_50x50mm_P32mm_611CB5AF_ln_015  label="D5_LED_WS2812B_PLCC4_50x50mm_P32mm_611CB5DD"
  LinkPlacement = pos=(127,19.05,-1.6) rot=(0,1,0;3.14159rad)
  LinkedObject = -> Shape005
  Placement = pos=(127,19.05,-1.6) rot=(0,1,0;3.14159rad)
FEATURE [App::Link] D3_LED_WS2812B_PLCC4_50x50mm_P32mm_611CB5AF_ln_016  label="D4_LED_WS2812B_PLCC4_50x50mm_P32mm_611CB5C6"
  LinkPlacement = pos=(69.85,19.05,-1.6) rot=(0,1,0;3.14159rad)
  LinkedObject = -> Shape005
  Placement = pos=(69.85,19.05,-1.6) rot=(0,1,0;3.14159rad)
FEATURE [App::Link] D3_LED_WS2812B_PLCC4_50x50mm_P32mm_611CB5AF_ln_017  label="D2_LED_WS2812B_PLCC4_50x50mm_P32mm_611E9F10"
  LinkPlacement = pos=(-44.45,19.05,-1.6) rot=(0,1,0;3.14159rad)
  LinkedObject = -> Shape005
  Placement = pos=(-44.45,19.05,-1.6) rot=(0,1,0;3.14159rad)
FEATURE [App::Link] D3_LED_WS2812B_PLCC4_50x50mm_P32mm_611CB5AF_ln_018  label="D1_LED_WS2812B_PLCC4_50x50mm_P32mm_611CB581"
  LinkPlacement = pos=(-101.6,19.05,-1.6) rot=(0,1,0;3.14159rad)
  LinkedObject = -> Shape005
  Placement = pos=(-101.6,19.05,-1.6) rot=(0,1,0;3.14159rad)
FEATURE [Part::Feature] Shape016  label="BZ1_Buzzer_Murata_PKMCS0909E4000_R1_611CB3F8"
  Placement = pos=(-23.019,0,-1.6) rot=(1,0,0;3.14159rad)
  shape: bbox 9 x 9 x 1.9 mm, 41 faces (baked)
FEATURE [App::Part] Bot_e1db
  Group = -> [Shape002,R7_R_0603_1608Metric_611CC01B_ln_,R7_R_0603_1608Metric_611CC01B_ln_001,R7_R_0603_1608Metric_611CC01B_ln_002,R7_R_0603_1608Metric_611CC01B_ln_003,R7_R_0603_1608Metric_611CC01B_ln_004,R7_R_0603_1608Metric_611CC01B_ln_005,R7_R_0603_1608Metric_611CC01B_ln_006,R7_R_0603_1608Metric_611CC01B_ln_007,R7_R_0603_1608Metric_611CC01B_ln_008,R7_R_0603_1608Metric_611CC01B_ln_009,+171 more]
  Origin = -> Origin004
FEATURE [App::Part] Step_Models_e1db
  Group = -> [Top_e1db,Bot_e1db]
  Origin = -> Origin002
FEATURE [Part::Feature] topSilks_dbf0
  Placement = pos=(-174.625,80.9625,0.07) rot=(0,0,1;0rad)
  shape: large baked B-rep (258 MB .brp); summary skipped
FEATURE [Part::Feature] botSilks_1a36
  Placement = pos=(-174.625,80.9625,-1.67) rot=(0,0,1;0rad)
  shape: large baked B-rep (64 MB .brp); summary skipped
FEATURE [Part::Feature] topTracks_e1db
  Placement = pos=(-174.625,80.9625,0.01) rot=(0,0,1;0rad)
  shape: bbox 335.5 x 119.6 x 0.04 mm, 420 faces, 0 solids (baked)
FEATURE [Part::Feature] botTracks_e1db
  Placement = pos=(-174.625,80.9625,-1.61) rot=(0,0,1;0rad)
  shape: bbox 335.5 x 119.6 x 0.04 mm, 1352 faces, 0 solids (baked)
FEATURE [App::Part] Board_Geoms_e1db
  Group = -> [Local_CS_e1db,Pcb_e1db,PCB_Sketch_e1db,topSilks_dbf0,botSilks_1a36,topTracks_e1db,botTracks_e1db]
  Origin = -> Origin
FEATURE [App::Part] Board_e1db  label="Orthonite87_PCB"
  Group = -> [Board_Geoms_e1db,Step_Models_e1db]
  Origin = -> Origin001
